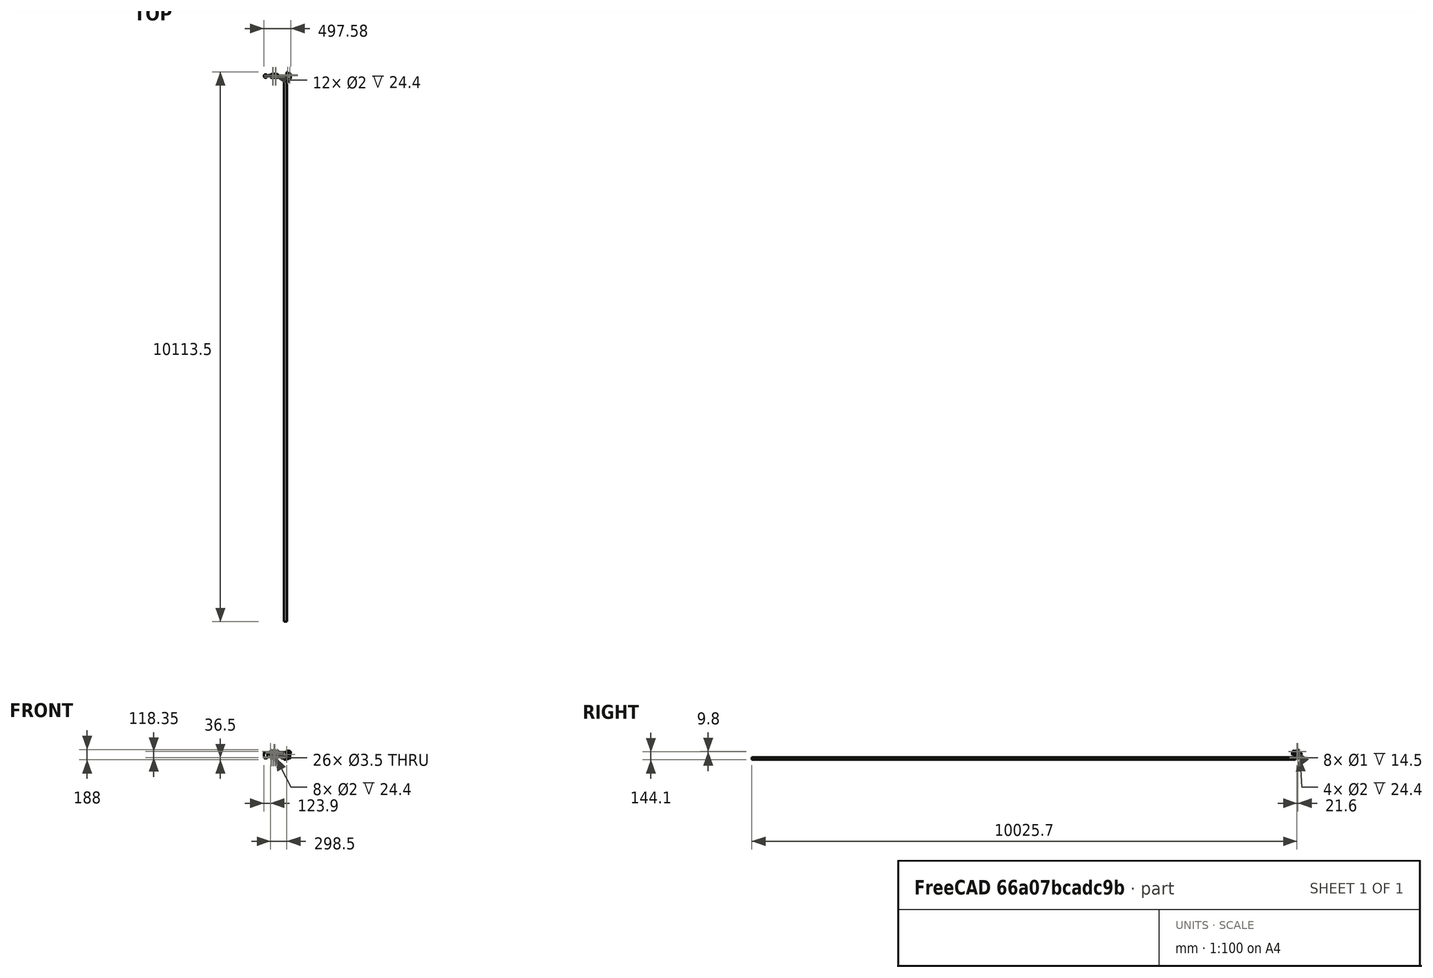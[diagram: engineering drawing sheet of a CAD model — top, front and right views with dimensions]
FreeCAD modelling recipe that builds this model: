
FCSTD DOCUMENT  (FreeCAD 0.15R4671 (Git))
Label: robot completo
License: CC-BY 3.0
LicenseURL: http://creativecommons.org/licenses/by/3.0/
objects: Part::Feature×135, Part::Box×79, Part::Cut×69, Part::Cylinder×67, Part::MultiFuse×45, Part::Fillet×16, Sketcher::SketchObject×16, Part::FeaturePython×12, PartDesign::Pad×11, App::DocumentObjectGroup×10, Part::Mirroring×10, Part::Prism×7, Part::Chamfer×6, PartDesign::Pocket×5, Part::Sphere×3, Mesh::Feature×3, PartDesign::Fillet×2
note: 499 computed .brp shape members not serialized (recipe doc carries the construction recipe); baked Part::Feature solids carry a one-line shape summary decoded from their .brp

FEATURE [Part::Feature] Part__Feature013  label="Servo-D1"
  Placement = pos=(26.5,9.5,100.6) rot=(0,1,0;3.14159rad)
  shape: bbox 55.5 x 20 x 41.74 mm, 365 faces (baked)
FEATURE [Part::Feature] Part__Feature014  label="Servo-D2"
  Placement = pos=(0,0,13) rot=(0.57735,0.57735,0.57735;2.0944rad)
  shape: bbox 41.74 x 55.5 x 20 mm, 365 faces (baked)
FEATURE [Part::Feature] Part__Feature008  label="J1"
  Placement = pos=(-10.8,44.37,77.54) rot=(0.707107,0.707107,0;3.14159rad)
  shape: bbox 11.7 x 15.49 x 2.5 mm, 224 faces (baked)
FEATURE [Part::Feature] Part__Feature009  label="J2"
  Placement = pos=(-10.8,62.15,77.54) rot=(0.707107,0.707107,0;3.14159rad)
  shape: bbox 11.7 x 15.49 x 2.5 mm, 224 faces (baked)
FEATURE [Part::Feature] Part__Feature007  label="J4"
  Placement = pos=(-10.8,59.6199,125.78) rot=(0,0,-1;1.5708rad)
  shape: bbox 11.65 x 20.57 x 2.5 mm, 290 faces (baked)
FEATURE [Part::Feature] Part__Feature010  label="J16"
  Placement = pos=(-9.55,7.19908,100.417) rot=(0.57735,0.57735,-0.57735;2.0944rad)
  shape: bbox 2.94 x 5.43 x 7.98 mm, 414 faces, 0 solids (baked)
FEATURE [Part::Feature] Part__Feature005  label="PCB"
  Placement = pos=(-12.3914,5,75) rot=(0.57735,0.57735,0.57735;2.0944rad)
  shape: bbox 1.591 x 68.6 x 53.36 mm, 426 faces (baked)
FEATURE [Part::Feature] Part__Feature004  label="J010"
  Placement = pos=(-10.8,14.8841,83.3059) rot=(0.707107,0.707107,0;3.14159rad)
  shape: bbox 10.92 x 14.61 x 8.89 mm, 41 faces (baked)
FEATURE [Part::Feature] Part__Feature011  label="U1"
  Placement = pos=(-9.2,12.159,115.511) rot=(0.57735,-0.57735,-0.57735;2.0944rad)
  shape: bbox 2.435 x 26.9 x 13 mm, 503 faces (baked)
FEATURE [Part::Feature] Part__Feature006  label="J8"
  Placement = pos=(-10.8,37.7759,125.78) rot=(0,0,-1;1.5708rad)
  shape: bbox 11.65 x 20.57 x 2.5 mm, 290 faces (baked)
FEATURE [App::DocumentObjectGroup] Group001  label="placa"
  Group = -> [Part__Feature008,Part__Feature009,Part__Feature007,Part__Feature010,Part__Feature005,Part__Feature004,Part__Feature011,Part__Feature006]
FEATURE [Part::Box] Box  label="Cube"
  Height = 24
  Length = 72
  Placement = pos=(-15,-29,-3) rot=(0,0,1;0rad)
  Width = 58
FEATURE [Part::Box] Box001  label="Cube001"
  Height = 25
  Length = 47
  Placement = pos=(-1,-21,2) rot=(0,0,1;0rad)
  Width = 42
FEATURE [Part::Box] Box002  label="Cube002"
  Height = 38
  Length = 28
  Placement = pos=(37,-45,1) rot=(0,0,1;0rad)
  Width = 88
FEATURE [Part::Box] Box003  label="Cube003"
  Height = 38
  Length = 28
  Placement = pos=(-33,-45,1) rot=(0,0,1;0rad)
  Width = 88
FEATURE [Part::Cut] Cut
  Base = -> Box
  Tool = -> Box001
FEATURE [Part::Cut] Cut001
  Base = -> Cut
  Tool = -> Box002
FEATURE [Part::Cut] Cut002
  Base = -> Cut001
  Tool = -> Box003
FEATURE [Part::Box] Box004  label="Cube004"
  Height = 60
  Length = 44
  Placement = pos=(-5,-24,-5) rot=(0,0,1;0rad)
  Width = 61
FEATURE [Part::Mirroring] Part__Mirroring  label="Servo-D1 (Mirror #1)"
  Base = (0,0,0)
  Normal = (0,1,0)
  Placement = pos=(0,72,0) rot=(0,0,1;0rad)
  Source = -> Part__Feature013
FEATURE [Part::Mirroring] Part__Mirroring001  label="Servo-D2 (Mirror #2)"
  Base = (0,0,0)
  Normal = (0,1,0)
  Placement = pos=(0,72,0) rot=(0,0,1;0rad)
  Source = -> Part__Feature014
FEATURE [Part::Cylinder] Cylinder003  label="Joint-D005"
  Angle = 360
  Height = 74.5
  Placement = pos=(-22,9.5,12) rot=(0,1,0;1.5708rad)
  Radius = 1.75
FEATURE [Part::Fillet] Fillet
  Base = -> Cut002
  Edges = 4 edges r=10: [Edge1,Edge3,Edge5,Edge14]
FEATURE [Part::Cylinder] Cylinder002  label="Joint-D004"
  Angle = 360
  Height = 53
  Placement = pos=(-9,9.5,12) rot=(0,1,0;1.5708rad)
  Radius = 10.5
FEATURE [Part::MultiFuse] Fusion
  Shapes = -> [Cylinder002]
FEATURE [Part::Cylinder] Cylinder004  label="Joint-D006"
  Angle = 360
  Height = 74.5
  Placement = pos=(16,9.5,12) rot=(0,1,0;1.5708rad)
  Radius = 5.5
FEATURE [Part::Cut] Cut003
  Base = -> Fusion
  Tool = -> Box004
FEATURE [Part::Cylinder] Cylinder005  label="Joint-D007"
  Angle = 360
  Height = 74.5
  Placement = pos=(-51,9.5,12) rot=(0,1,0;1.5708rad)
  Radius = 1.75
FEATURE [Part::Cut] Cut004
  Base = -> Cut003
  Tool = -> Cylinder004
FEATURE [Part::Cut] Cut005
  Base = -> Cut004
  Tool = -> Cylinder005
FEATURE [Part::Cylinder] Cylinder006  label="Joint-D008"
  Angle = 360
  Height = 74.5
  Placement = pos=(41.8,9.5,12) rot=(0,1,0;1.5708rad)
  Radius = 11
FEATURE [Part::Cut] Cut006
  Base = -> Cut005
  Tool = -> Cylinder006
FEATURE [Part::Cylinder] Cylinder007  label="Joint-D009"
  Angle = 360
  Height = 23.5
  Placement = pos=(16.8,9.5,58.3) rot=(0,1,0;3.14159rad)
  Radius = 11
FEATURE [Part::Cylinder] Cylinder008  label="Joint-D010"
  Angle = 360
  Height = 21.5
  Placement = pos=(16,-24.5,7) rot=(0,1,0;1.5708rad)
  Radius = 1.75
FEATURE [Part::Cylinder] Cylinder009  label="Joint-D011"
  Angle = 360
  Height = 21.5
  Placement = pos=(32,-24.5,7) rot=(0,1,0;1.5708rad)
  Radius = 3
FEATURE [Part::MultiFuse] Fusion001
  Shapes = -> [Cylinder009,Cylinder008]
FEATURE [Part::MultiFuse] Fusion002
  Placement = pos=(0,0,10) rot=(0,0,1;0rad)
  Shapes = -> [Cylinder009,Cylinder008]
FEATURE [Part::MultiFuse] Fusion003
  Placement = pos=(0,49,0) rot=(0,0,1;0rad)
  Shapes = -> [Cylinder009,Cylinder008]
FEATURE [Part::MultiFuse] Fusion004
  Placement = pos=(0,49,10) rot=(0,0,1;0rad)
  Shapes = -> [Cylinder009,Cylinder008]
FEATURE [Part::Box] Box006  label="Cube006"
  Height = 21
  Length = 4
  Placement = pos=(25.5,-28,2) rot=(0,0,1;0rad)
  Width = 56
FEATURE [Part::Cylinder] Cylinder010  label="Joint-D012"
  Angle = 360
  Height = 74.5
  Placement = pos=(17,9.5,12) rot=(0,0,1;0rad)
  Radius = 5.5
FEATURE [Part::Box] Box007  label="Cube007"
  Height = 6
  Length = 3
  Placement = pos=(18.5,-28,4) rot=(0,0,1;0rad)
  Width = 56
FEATURE [Part::Box] Box008  label="Cube008"
  Height = 6
  Length = 3
  Placement = pos=(18.5,-28,14) rot=(0,0,1;0rad)
  Width = 56
FEATURE [Part::Cylinder] Cylinder011  label="Joint-D013"
  Angle = 360
  Height = 74.5
  Placement = pos=(-3,9.5,12) rot=(0,1,0;1.5708rad)
  Radius = 2.75
FEATURE [Part::Box] Box009  label="Cube009"
  Height = 5
  Length = 80
  Placement = pos=(-23,-4,63) rot=(0,0,1;0rad)
  Width = 80
FEATURE [Part::Box] Box010  label="Cube010"
  Height = 9
  Length = 7
  Placement = pos=(-1,-1,63) rot=(0,0,1;0rad)
  Width = 74
FEATURE [Part::Box] Box011  label="Cube011"
  Height = 9
  Length = 7
  Placement = pos=(47,-1,63) rot=(0,0,1;0rad)
  Width = 74
FEATURE [Part::MultiFuse] Fusion005
  Placement = pos=(44,39,98) rot=(0,1,0;1.5708rad)
  Shapes = -> [Cylinder009,Cylinder008]
FEATURE [Part::MultiFuse] Fusion008
  Placement = pos=(44,29,98) rot=(0,1,0;1.5708rad)
  Shapes = -> [Cylinder009,Cylinder008]
FEATURE [Part::MultiFuse] Fusion009
  Placement = pos=(-5,39,98) rot=(0,1,0;1.5708rad)
  Shapes = -> [Cylinder009,Cylinder008]
FEATURE [Part::MultiFuse] Fusion010
  Placement = pos=(-5,29,98) rot=(0,1,0;1.5708rad)
  Shapes = -> [Cylinder009,Cylinder008]
FEATURE [Part::Box] Box012  label="Cube012"
  Height = 9
  Length = 70
  Placement = pos=(-6,8.5,70) rot=(0,0,1;0rad)
  Width = 2
FEATURE [Part::MultiFuse] Fusion011
  Shapes = -> [Box012,Fusion009,Fusion010,Fusion008,Fusion005]
FEATURE [Part::MultiFuse] Fusion012
  Placement = pos=(0,53,0) rot=(0,0,1;0rad)
  Shapes = -> [Box012,Fusion009,Fusion010,Fusion008,Fusion005]
FEATURE [Part::MultiFuse] Fusion013
  Shapes = -> [Box009,Box011,Box010]
FEATURE [Part::Cut] Cut018
  Base = -> Fusion013
  Tool = -> Fusion012
FEATURE [Part::Cut] Cut019
  Base = -> Cut018
  Tool = -> Fusion011
FEATURE [Part::Box] Box014  label="Cube014"
  Height = 43
  Length = 41
  Placement = pos=(6,-1,59) rot=(0,0,1;0rad)
  Width = 21
FEATURE [Part::Box] Box015  label="Cube015"
  Height = 43
  Length = 41
  Placement = pos=(6,52,59) rot=(0,0,1;0rad)
  Width = 21
FEATURE [Part::Cut] Cut020
  Base = -> Cut019
  Tool = -> Box014
FEATURE [Part::Cut] Cut021
  Base = -> Cut020
  Tool = -> Box015
FEATURE [Part::Box] Box016  label="Cube016"
  Height = 12
  Length = 6
  Placement = pos=(-11.5,3,69) rot=(0,0,1;0rad)
  Width = 3
FEATURE [Part::Box] Box017  label="Cube017"
  Height = 12
  Length = 16
  Placement = pos=(-20,-1,63) rot=(0,0,1;0rad)
  Width = 74
FEATURE [Part::Box] Box018  label="Cube018"
  Height = 12
  Length = 6
  Placement = pos=(-11.5,66,69) rot=(0,0,1;0rad)
  Width = 3
FEATURE [Part::MultiFuse] Fusion014
  Shapes = -> [Cut021,Box017]
FEATURE [Part::Cut] Cut022
  Base = -> Fusion014
  Tool = -> Box016
FEATURE [Part::Cut] Cut023
  Base = -> Cut022
  Tool = -> Box018
FEATURE [PartDesign::Fillet] Fillet011  label="horn"
  Placement = pos=(38.5,9.5,13) rot=(0,0,-1;1.5708rad)
  Radius = 0.5
FEATURE [Part::Cylinder] Cylinder021  label="Joint-D014"
  Angle = 360
  Height = 52.5
  Placement = pos=(19,9.5,20.35) rot=(0,1,0;1.5708rad)
  Radius = 1
FEATURE [Part::Cylinder] Cylinder022  label="Joint-D015"
  Angle = 360
  Height = 52.5
  Placement = pos=(19,2,9.5) rot=(0,1,0;1.5708rad)
  Radius = 1
FEATURE [Part::Cylinder] Cylinder023  label="Joint-D016"
  Angle = 360
  Height = 52.5
  Placement = pos=(19,17,9.5) rot=(0,1,0;1.5708rad)
  Radius = 1
FEATURE [Part::MultiFuse] Fusion017
  Placement = pos=(0,0,-1) rot=(0,0,1;0rad)
  Shapes = -> [Cylinder022,Cylinder021,Cylinder023]
FEATURE [Part::MultiFuse] Fusion018
  Placement = pos=(4,0,101) rot=(0,1,0;1.5708rad)
  Shapes = -> [Cylinder022,Cylinder021,Cylinder023]
FEATURE [PartDesign::Fillet] Fillet012  label="horn001"
  Placement = pos=(16.8,9.5,62.5) rot=(-0.57735,0.57735,-0.57735;2.0944rad)
  Radius = 0.5
FEATURE [Part::Mirroring] Part__Mirroring003  label="horn (Mirror #4)"
  Base = (41.6,1.90735e-06,13)
  Normal = (0,1,-1.19209e-07)
  Placement = pos=(0,72,0) rot=(0,0,1;0rad)
  Source = -> Fillet011
FEATURE [Part::Mirroring] Part__Mirroring004  label="horn001 (Mirror #5)"
  Base = (16.8,7.62939e-06,59.3998)
  Normal = (0,1,-1.19209e-07)
  Placement = pos=(0,72,0) rot=(0,0,1;0rad)
  Source = -> Fillet012
FEATURE [Part::Chamfer] Chamfer
  Base = -> Fillet
  Edges = 3 edges r=3: [Edge18,Edge33,Edge37]
FEATURE [Part::Cut] Cut008
  Base = -> Chamfer
  Tool = -> Cylinder003
FEATURE [Part::Cut] Cut010
  Base = -> Cut008
  Tool = -> Box006
FEATURE [Part::Cut] Cut011
  Base = -> Cut010
  Tool = -> Box008
FEATURE [Part::Cut] Cut012
  Base = -> Cut011
  Tool = -> Box007
FEATURE [Part::Cut] Cut013
  Base = -> Cut012
  Tool = -> Fusion004
FEATURE [Part::Cut] Cut014
  Base = -> Cut013
  Tool = -> Fusion003
FEATURE [Part::Cut] Cut015
  Base = -> Cut014
  Tool = -> Fusion002
FEATURE [Part::Cut] Cut016
  Base = -> Cut015
  Tool = -> Fusion001
FEATURE [Part::Cut] Cut017  label="pie"
  Base = -> Cut016
  Tool = -> Cylinder011
FEATURE [Part::Box] Box024  label="Cube024"
  Height = 23
  Length = 6
  Placement = pos=(0,19,7) rot=(0,0,1;0rad)
  Width = 36
FEATURE [Part::Cut] Cut039  label="pie-D"
  Base = -> Cut017
  Placement = pos=(0,0,1) rot=(0,0,1;0rad)
  Tool = -> Box024
FEATURE [Part::Mirroring] Part__Mirroring006  label="pie-I"
  Base = (0,0,0)
  Normal = (0,1,0)
  Placement = pos=(0,72,0) rot=(0,0,1;0rad)
  Source = -> Cut039
FEATURE [Part::Cut] Cut044
  Base = -> Cut006
  Tool = -> Box004
FEATURE [Part::Cut] Cut045
  Base = -> Cut044
  Tool = -> Cylinder007
FEATURE [Part::Cut] Cut046
  Base = -> Cut045
  Tool = -> Fusion018
FEATURE [Part::Cut] Cut047
  Base = -> Cut046
  Tool = -> Fusion017
FEATURE [Part::Cut] Cut048
  Base = -> Cut047
  Placement = pos=(0,0,1) rot=(0,0,1;0rad)
  Tool = -> Cylinder010
FEATURE [Part::Chamfer] Chamfer001
  Base = -> Cut048
  Edges = 1 edges r=4: [Edge61]
FEATURE [Part::Chamfer] Chamfer002  label="pata-D"
  Base = -> Chamfer001
  Edges = 1 edges r=8: [Edge58]
FEATURE [Part::Mirroring] Part__Mirroring007  label="pata-I"
  Base = (17.5,3.8147e-06,32.25)
  Normal = (0,1,-1.19209e-07)
  Placement = pos=(0,72,0) rot=(0,0,1;0rad)
  Source = -> Chamfer002
FEATURE [Part::Cylinder] Cylinder012  label="Cylinder030"
  Angle = 360
  Height = 31
  Placement = pos=(-8.5,92,71.5) rot=(1,0,0;1.5708rad)
  Radius = 1.75
FEATURE [Part::Cut] Cut024
  Base = -> Cut023
  Tool = -> Cylinder012
FEATURE [Part::Cylinder] Cylinder013  label="Cylinder001"
  Angle = 360
  Height = 31
  Placement = pos=(-8.5,11,71.5) rot=(1,0,0;1.5708rad)
  Radius = 1.75
FEATURE [Part::Feature] Part__Feature  label="Portapilas008"
  shape: bbox 2e-07 x 47.97 x 51.59 mm, 1 faces, 0 solids (baked)
FEATURE [Part::Feature] Part__Feature015  label="Portapilas007"
  shape: bbox 9.213 x 1.1 x 48.01 mm, 3 faces, 0 solids (baked)
FEATURE [Part::Feature] Part__Feature016  label="Portapilas006"
  shape: bbox 9.213 x 1.1 x 48.01 mm, 3 faces, 0 solids (baked)
FEATURE [Part::Feature] Part__Feature017  label="Portapilas005"
  shape: bbox 9.213 x 1.1 x 48.01 mm, 3 faces, 0 solids (baked)
FEATURE [Part::Feature] Part__Feature018  label="Portapilas004"
  shape: bbox 9.213 x 1.1 x 48.01 mm, 3 faces, 0 solids (baked)
FEATURE [Part::Feature] Part__Feature019  label="Portapilas003"
  shape: bbox 9.213 x 1.1 x 48.01 mm, 3 faces, 0 solids (baked)
FEATURE [Part::Feature] Part__Feature020  label="Portapilas002"
  shape: bbox 9.213 x 1.1 x 48.01 mm, 3 faces, 0 solids (baked)
FEATURE [Part::Feature] Part__Feature021  label="Portapilas001"
  shape: bbox 16.42 x 48.04 x 51.59 mm, 26 faces, 0 solids (baked)
FEATURE [Part::Feature] Part__Feature022  label="Portapilas"
  shape: bbox 21.03 x 69.14 x 72.63 mm, 394 faces, 0 solids (baked)
FEATURE [Part::MultiFuse] Fusion019  label="peterpilas"
  Placement = pos=(23,77.5,76) rot=(0,0,1;1.5708rad)
  Shapes = -> [Part__Feature022,Part__Feature021,Part__Feature020,Part__Feature019,Part__Feature018,Part__Feature017,Part__Feature016,Part__Feature015,Part__Feature]
FEATURE [Part::Feature] Part__Feature023  label="Ultrasonido_BAT"
  Placement = pos=(-17,36,59.5) rot=(0,0,1;0rad)
  shape: bbox 18.72 x 56 x 27.52 mm, 81 faces (baked)
FEATURE [Part::Cut] Cut050
  Base = -> Cut024
  Tool = -> Cylinder013
FEATURE [Part::Box] Box032  label="Cube032"
  Height = 20
  Length = 3
  Placement = pos=(51,20,66) rot=(0,0,1;0rad)
  Width = 32
FEATURE [Part::Box] Box033  label="Cube033"
  Height = 54
  Length = 4.5
  Placement = pos=(-20,6,64) rot=(0,0,1;0rad)
  Width = 60
FEATURE [Part::Box] Box035  label="Cube035"
  Height = 68
  Length = 6
  Placement = pos=(-23.5,17,68) rot=(0,0,1;0rad)
  Width = 38
FEATURE [Part::Box] Box036  label="Cube034"
  Height = 17
  Length = 13
  Placement = pos=(-14,20,62) rot=(0,0,1;0rad)
  Width = 32
FEATURE [Part::Fillet] Fillet018002
  Base = -> Box036
  Edges = 4 edges r=5: [Edge1,Edge3,Edge5,Edge7]
FEATURE [Part::Cylinder] Cylinder  label="Cylinder094"
  Angle = 360
  Height = 31
  Placement = pos=(-49.5,29,111.5) rot=(0,1,0;1.5708rad)
  Radius = 1.75
FEATURE [Part::Cylinder] Cylinder040  label="Cylinder095"
  Angle = 360
  Height = 31
  Placement = pos=(-49.5,49,91.5) rot=(0,1,0;1.5708rad)
  Radius = 1.75
FEATURE [Part::Cylinder] Cylinder041  label="Cylinder096"
  Angle = 360
  Height = 31
  Placement = pos=(-49.5,49,111.5) rot=(0,1,0;1.5708rad)
  Radius = 1.75
FEATURE [Part::MultiFuse] Fusion025
  Shapes = -> [Box032,Cut050]
FEATURE [Part::Box] Box037  label="Cube036"
  Height = 44
  Length = 61
  Placement = pos=(-9,22,66) rot=(0,0,1;0rad)
  Width = 28
FEATURE [Part::MultiFuse] Fusion026
  Shapes = -> [Fusion025,Box033]
FEATURE [Part::Cut] Cut051
  Base = -> Fusion026
  Tool = -> Fillet018002
FEATURE [Part::Box] Box038  label="Cube037"
  Height = 11
  Length = 8
  Placement = pos=(-11.5,-52,95) rot=(0,0,1;0rad)
  Width = 58
FEATURE [Part::Cylinder] Cylinder042  label="Cylinder097"
  Angle = 360
  Height = 61
  Placement = pos=(-5,124,89.6) rot=(1,0,0;1.5708rad)
  Radius = 4
FEATURE [Part::Cylinder] Cylinder043  label="Cylinder098"
  Angle = 360
  Height = 63
  Placement = pos=(-3,11,83.5) rot=(1,0,0;1.5708rad)
  Radius = 6
FEATURE [Part::Box] Box039  label="Cube038"
  Height = 66
  Length = 76
  Placement = pos=(-21,-2,63) rot=(0,0,1;0rad)
  Width = 76
FEATURE [Part::Cylinder] Cylinder044  label="Cylinder099"
  Angle = 360
  Height = 23
  Placement = pos=(-8.5,1,71.5) rot=(1,0,0;1.5708rad)
  Radius = 1.75
FEATURE [Part::Cylinder] Cylinder045  label="Cylinder100"
  Angle = 360
  Height = 31
  Placement = pos=(-8.5,94,71.5) rot=(1,0,0;1.5708rad)
  Radius = 1.75
FEATURE [Part::Fillet] Fillet018007
  Base = -> Box039
  Edges = 8 edges r=3: [Edge1,Edge2,Edge3,Edge5,Edge6,Edge7,Edge10,Edge12]
FEATURE [Part::Box] Box040  label="Cube039"
  Height = 6
  Length = 81
  Placement = pos=(-23.5,-4.5,63) rot=(0,0,1;0rad)
  Width = 81
FEATURE [Part::Fillet] Fillet018008
  Base = -> Box040
  Edges = 4 edges r=5: [Edge1,Edge3,Edge5,Edge7]
  Placement = pos=(0,0,-1) rot=(0,0,1;0rad)
FEATURE [Part::Cylinder] Cylinder046  label="Cylinder101"
  Angle = 360
  Height = 45
  Placement = pos=(-8.5,-7,71.5) rot=(1,0,0;1.5708rad)
  Radius = 4
FEATURE [Part::Cylinder] Cylinder047  label="Cylinder102"
  Angle = 360
  Height = 45
  Placement = pos=(-8.5,124,71.5) rot=(1,0,0;1.5708rad)
  Radius = 4
FEATURE [Part::MultiFuse] Fusion033
  Shapes = -> [Fillet018007,Fillet018008]
FEATURE [Part::MultiFuse] Fusion034  label="corte-positivo"
  Shapes = -> [Fusion033,Cylinder042,Cylinder047,Cylinder045,Cylinder046,Cylinder043,Box038,Cylinder044]
FEATURE [Part::Cylinder] Cylinder053  label="Cylinder103"
  Angle = 360
  Height = 31
  Placement = pos=(-49.5,29,91.5) rot=(0,1,0;1.5708rad)
  Radius = 1.75
FEATURE [Part::MultiFuse] Fusion038
  Placement = pos=(14,0,0) rot=(0,0,1;0rad)
  Shapes = -> [Cylinder053,Cylinder040,Cylinder041,Cylinder]
FEATURE [App::DocumentObjectGroup] Group004  label="electronic"
  Group = -> [Part__Mirroring,Part__Mirroring001,Part__Mirroring003,Part__Mirroring004,Fusion019,Part__Feature023,Group001]
FEATURE [App::DocumentObjectGroup] Group005  label="aux"
  Group = -> [Fusion034]
FEATURE [Part::Cut] Cut066
  Base = -> Cut051
  Tool = -> Box037
FEATURE [Part::Chamfer] Chamfer003
  Base = -> Cut066
  Edges = 1 edges r=3: [Edge86]
FEATURE [Sketcher::SketchObject] Sketch
  Placement = pos=(-22,0,0) rot=(0.57735,-0.57735,-0.57735;2.0944rad)
  sketch-geometry (4):
    g0: ArcOfCircle CenterX=-49 CenterY=111.5 CenterZ=0 NormalX=0 NormalY=0 NormalZ=1 Radius=3.5 StartAngle=9.1497e-08 EndAngle=3.14159
    g1: LineSegment StartX=-52.5 StartY=111.5 StartZ=0 EndX=-52.5 EndY=91.5 EndZ=0
    g2: LineSegment StartX=-45.5 StartY=111.5 StartZ=0 EndX=-45.5 EndY=91.5 EndZ=0
    g3: ArcOfCircle CenterX=-49 CenterY=91.5 CenterZ=0 NormalX=0 NormalY=0 NormalZ=1 Radius=3.5 StartAngle=3.14159 EndAngle=6.28319
  constraints (13):
    c: DistanceX(g-1,g0) = -49
    c: DistanceY(g-1,g0) = 111.5
    c: Radius(g0) = 3.5
    c: Vertical(g1)
    c: Vertical(g2)
    c: Coincident(g1,g0)
    c: Coincident(g2,g0)
    c: Tangent(g2,g0)
    c: Tangent(g1,g0)
    c: Coincident(g3,g1)
    c: Coincident(g3,g2)
    c: Equal(g3,g0)
    c: Distance(g3,g0) = 20
FEATURE [PartDesign::Pad] Pad
  Length = 5
  Length2 = 100
  Placement = pos=(-22,0,0) rot=(0.57735,-0.57735,-0.57735;2.0944rad)
  Reversed = true
  Sketch = -> Sketch
  Type = 0
FEATURE [Part::FeaturePython] Clone  label="Clone of Pad"  # Draft clone (typed FeaturePython)
  Objects = -> [Pad]
  Placement = pos=(-22,-20,0) rot=(0.57735,-0.57735,-0.57735;2.0944rad)
  Scale = (1,1,1)
FEATURE [Part::MultiFuse] Fusion039
  Placement = pos=(4.5,0,0) rot=(0,0,1;0rad)
  Shapes = -> [Pad,Clone]
FEATURE [Part::MultiFuse] Fusion040
  Shapes = -> [Chamfer003,Fusion039]
FEATURE [Part::Cut] Cut067
  Base = -> Fusion040
  Tool = -> Fusion038
FEATURE [Part::Cut] Cut068
  Base = -> Cut067
  Tool = -> Box035
FEATURE [Sketcher::SketchObject] Sketch001  label="leg-sketch-1"
  Placement = pos=(0,0,0) rot=(0.57735,0.57735,0.57735;2.0944rad)
  sketch-geometry (5):
    g0: LineSegment StartX=-49 StartY=10.5 StartZ=0 EndX=0 EndY=10.5 EndZ=0
    g1: LineSegment StartX=0 StartY=10.5 StartZ=0 EndX=0 EndY=-10.5 EndZ=0
    g2: LineSegment StartX=0 StartY=-10.5 StartZ=0 EndX=-49 EndY=-10.5 EndZ=0
    g3: LineSegment [constr] StartX=-49 StartY=-10.5 StartZ=0 EndX=-49 EndY=10.5 EndZ=0
    g4: ArcOfCircle CenterX=-49 CenterY=0 CenterZ=0 NormalX=0 NormalY=0 NormalZ=1 Radius=10.5 StartAngle=1.5708 EndAngle=4.71239
  constraints (15):
    c: Coincident(g0,g1)
    c: Coincident(g1,g2)
    c: Coincident(g2,g3)
    c: Coincident(g3,g0)
    c: Horizontal(g0)
    c: Horizontal(g2)
    c: Vertical(g1)
    c: Vertical(g3)
    c: PointOnObject(g4,g3)
    c: Coincident(g4,g0)
    c: Coincident(g4,g2)
    c: PointOnObject(g4,g-1)
    c: PointOnObject(g0,g-2)
    c: DistanceX(g0) = 49
    c: DistanceY(g1) = -21
FEATURE [PartDesign::Pad] Pad001  label="leg-block-1"
  Length = 53
  Length2 = 100
  Midplane = true
  Placement = pos=(0,0,0) rot=(0.57735,0.57735,0.57735;2.0944rad)
  Sketch = -> Sketch001
  Type = 0
FEATURE [Sketcher::SketchObject] Sketch002  label="leg-top-sketch"
  ExternalGeometry = -> [Pad001]
  Placement = pos=(0,0,10.5) rot=(0,0,-1;1.5708rad)
  Support = -> Pad001 [Face1]
  sketch-geometry (9):
    g0: LineSegment StartX=64 StartY=21.5 StartZ=0 EndX=10 EndY=21.5 EndZ=0
    g1: LineSegment StartX=6 StartY=17.5 StartZ=0 EndX=6 EndY=-19.5 EndZ=0
    g2: LineSegment StartX=9 StartY=-22.5 StartZ=0 EndX=64 EndY=-22.5 EndZ=0
    g3: LineSegment StartX=64 StartY=-22.5 StartZ=0 EndX=64 EndY=21.5 EndZ=0
    g4: LineSegment StartX=6 StartY=17.5 StartZ=0 EndX=10 EndY=21.5 EndZ=0
    g5: LineSegment [constr] StartX=6 StartY=17.5 StartZ=0 EndX=6 EndY=21.5 EndZ=0
    g6: LineSegment StartX=6 StartY=-19.5 StartZ=0 EndX=9 EndY=-22.5 EndZ=0
    g7: LineSegment [constr] StartX=9 StartY=-22.5 StartZ=0 EndX=6 EndY=-22.5 EndZ=0
    g8: LineSegment [constr] StartX=6 StartY=-22.5 StartZ=0 EndX=6 EndY=-19.5 EndZ=0
  constraints (26):
    c: Coincident(g2,g3)
    c: Coincident(g3,g0)
    c: Horizontal(g0)
    c: Horizontal(g2)
    c: Vertical(g1)
    c: Vertical(g3)
    c: DistanceY(g-3,g5) = -5
    c: DistanceY(g7,g-4) = -4
    c: Angle(g-2,g4) = 2.35619
    c: Coincident(g1,g4)
    c: Coincident(g5,g1)
    c: Vertical(g5)
    c: DistanceY(g1,g7) = -40
    c: DistanceX(g5,g-3) = -6
    c: Coincident(g0,g4)
    c: PointOnObject(g5,g0)
    c: DistanceX(g-3,g0) = 15
    c: Coincident(g2,g6)
    c: Coincident(g7,g2)
    c: Horizontal(g7)
    c: DistanceX(g7) = -3
    c: Coincident(g1,g6)
    c: Coincident(g8,g7)
    c: Coincident(g8,g1)
    c: Equal(g8,g7)
    c: Vertical(g8)
FEATURE [PartDesign::Pocket] Pocket  label="leg-block-2"
  Length = 5
  Placement = pos=(0,0,0) rot=(0.57735,0.57735,0.57735;2.0944rad)
  Sketch = -> Sketch002
  Type = 1
FEATURE [Sketcher::SketchObject] Sketch003  label="ankle-rounded-horn-sketch"
  ExternalGeometry = -> [Pocket]
  Placement = pos=(26.5,0,0) rot=(0.57735,0.57735,0.57735;2.0944rad)
  Support = -> Pocket [Face4]
  sketch-geometry (1):
    g0: Circle CenterX=-49 CenterY=0 CenterZ=0 NormalX=0 NormalY=0 NormalZ=1 Radius=10.75
  constraints (2):
    c: Coincident(g0,g-3)
    c: Radius(g0) = 10.75
FEATURE [PartDesign::Pocket] Pocket001  label="ankle-rounded-horn-cutout"
  Length = 2.2
  Placement = pos=(0,0,0) rot=(0.57735,0.57735,0.57735;2.0944rad)
  Sketch = -> Sketch003
  Type = 0
FEATURE [Sketcher::SketchObject] Sketch004  label="ankle-rear-shaft-drill-sketch"
  ExternalGeometry = -> [Pocket001]
  Placement = pos=(-26.5,0,0) rot=(0.57735,0.57735,-0.57735;4.18879rad)
  Support = -> Pocket001 [Face2]
  sketch-geometry (1):
    g0: Circle CenterX=-49 CenterY=0 CenterZ=0 NormalX=0 NormalY=0 NormalZ=1 Radius=1.75
  constraints (2):
    c: Coincident(g0,g-3)
    c: Radius(g0) = 1.75
FEATURE [PartDesign::Pocket] Pocket002  label="ankle-rear-shaft-drill"
  Length = 0
  Placement = pos=(0,0,0) rot=(0.57735,0.57735,0.57735;2.0944rad)
  Sketch = -> Sketch004
  Type = 2
FEATURE [Sketcher::SketchObject] Sketch005  label="hip-rounded-horn-cutout-sketch"
  Placement = pos=(0,-6,0) rot=(-0.57735,-0.57735,0.57735;4.18879rad)
  Support = -> Pocket002 [Face10]
  sketch-geometry (1):
    g0: Circle CenterX=0 CenterY=0 CenterZ=0 NormalX=0 NormalY=0 NormalZ=1 Radius=11
  constraints (2):
    c: Coincident(g0,g-1)
    c: Radius(g0) = 11
FEATURE [PartDesign::Pocket] Pocket003  label="hip-rounded-horn-cutout"
  Length = 3.3
  Placement = pos=(0,0,0) rot=(0.57735,0.57735,0.57735;2.0944rad)
  Sketch = -> Sketch005
  Type = 0
FEATURE [Sketcher::SketchObject] Sketch006  label="horn-side-chamfer-sketch"
  ExternalGeometry = -> [Pocket003]
  Placement = pos=(0,0,10.5) rot=(0,0,-1;1.5708rad)
  Support = -> Pocket003 [Face1]
  sketch-geometry (3):
    g0: LineSegment StartX=0 StartY=18.5 StartZ=0 EndX=8 EndY=26.5 EndZ=0
    g1: LineSegment StartX=0 StartY=18.5 StartZ=0 EndX=0 EndY=26.5 EndZ=0
    g2: LineSegment StartX=0 StartY=26.5 StartZ=0 EndX=8 EndY=26.5 EndZ=0
  constraints (8):
    c: PointOnObject(g0,g-2)
    c: PointOnObject(g0,g-3)
    c: Angle(g-2,g0) = 2.35619
    c: DistanceY(g-3,g0) = -8
    c: Coincident(g0,g1)
    c: Coincident(g1,g-3)
    c: Coincident(g1,g2)
    c: Coincident(g2,g0)
FEATURE [PartDesign::Pocket] Pocket004  label="horn-side-chamfer"
  Length = 5
  Placement = pos=(0,0,0) rot=(0.57735,0.57735,0.57735;2.0944rad)
  Sketch = -> Sketch006
  Type = 1
FEATURE [Part::Cylinder] Cylinder054  label="servo-shaft-drill"
  Angle = 360
  Height = 20
  Placement = pos=(0,10,0) rot=(1,0,0;1.5708rad)
  Radius = 5.5
FEATURE [Part::Cylinder] Cylinder055  label="servo-horn-small-drill-master"
  Angle = 360
  Height = 20
  Placement = pos=(-3.5,10,7.5) rot=(1,0,0;1.5708rad)
  Radius = 1
FEATURE [Part::FeaturePython] Clone001  label="Clone of servo-horn-small-drill-master"  # Draft clone (typed FeaturePython)
  Objects = -> [Cylinder055]
  Placement = pos=(7.35,10,-2.33815e-06) rot=(1,0,0;1.5708rad)
  Scale = (1,1,1)
FEATURE [Part::FeaturePython] Clone002  label="Clone of servo-horn-small-drill-master001"  # Draft clone (typed FeaturePython)
  Objects = -> [Cylinder055]
  Placement = pos=(-3.5,10,-7.5) rot=(1,0,0;1.5708rad)
  Scale = (1,1,1)
FEATURE [Part::MultiFuse] Fusion041  label="servo-Drills-block1-master"
  Shapes = -> [Clone001,Clone002,Cylinder055,Cylinder054]
FEATURE [Part::FeaturePython] Clone003  label="Clone of servo-Drills-block1-master"  # Draft clone (typed FeaturePython)
  Objects = -> [Fusion041]
  Placement = pos=(22,-49,6.96015e-06) rot=(0,0,1;1.5708rad)
  Scale = (1,1,1)
FEATURE [Part::MultiFuse] Fusion042  label="Servo-horn-drills"
  Shapes = -> [Fusion041,Clone003]
FEATURE [Part::Cut] Cut070  label="Leg"
  Base = -> Pocket004
  Tool = -> Fusion042
FEATURE [App::DocumentObjectGroup] Group007  label="Leg-src"
  Group = -> [Pad001,Pocket,Pocket001,Pocket002,Pocket003,Cut070]
FEATURE [App::DocumentObjectGroup] Group006  label="src"
  Group = -> [Group007]
FEATURE [Part::Feature] Fusion043  label="soft-drink-can"
  Placement = pos=(-397.85,47.19,0) rot=(0,0,-1;1.5708rad)
  shape: bbox 66.1 x 66.1 x 115.2 mm, 53 faces (baked)
FEATURE [App::DocumentObjectGroup] Group018  label="development"
  Group = -> [Group006]
FEATURE [Part::Fillet] Fillet018013  label="chass"
  Base = -> Cut068
  Edges = 4 edges r=3: [Edge75,Edge118,Edge216,Edge229]
FEATURE [Sketcher::SketchObject] Sketch010
  Placement = pos=(-1,0,0) rot=(0.57735,0.57735,0.57735;2.0944rad)
  sketch-geometry (5):
    g0: LineSegment StartX=-35.7295 StartY=116.767 StartZ=0 EndX=-15.7739 EndY=107.988 EndZ=0
    g1: LineSegment StartX=-7.00034 StartY=107.988 StartZ=0 EndX=-7.00034 EndY=136.643 EndZ=0
    g2: LineSegment StartX=-7.00034 StartY=136.643 StartZ=0 EndX=-31.551 EndY=136.643 EndZ=0
    g3: ArcOfCircle CenterX=-31.551 CenterY=126.266 CenterZ=0 NormalX=0 NormalY=0 NormalZ=1 Radius=10.3774 StartAngle=1.5708 EndAngle=4.29797
    g4: LineSegment StartX=-15.7739 StartY=107.988 StartZ=0 EndX=-7.00034 EndY=107.988 EndZ=0
  constraints (10):
    c: Coincident(g1,g2)
    c: Coincident(g2,g3)
    c: Coincident(g0,g3)
    c: Horizontal(g2)
    c: Vertical(g1)
    c: Tangent(g3,g0)
    c: Tangent(g3,g2)
    c: Coincident(g1,g4)
    c: Coincident(g0,g4)
    c: Horizontal(g4)
FEATURE [PartDesign::Pad] Pad005
  Length = 42
  Length2 = 100
  Placement = pos=(-1,0,0) rot=(0.57735,0.57735,0.57735;2.0944rad)
  Sketch = -> Sketch010
  Type = 0
FEATURE [Part::MultiFuse] Fusion045  label="servo-src"
  Placement = pos=(23,4.5,120) rot=(0,0.707107,-0.707107;3.14159rad)
  Shapes = -> [Part__Feature,Part__Feature004,Part__Feature005]
FEATURE [Part::FeaturePython] Clone007  label="microservo"  # Draft clone (typed FeaturePython)
  Objects = -> [Fusion045]
  Placement = pos=(-207.5,47,122.5) rot=(0.57735,0.57735,0.57735;2.0944rad)
  Scale = (1,1,1)
FEATURE [Part::FeaturePython] Clone008  label="microservo001"  # Draft clone (typed FeaturePython)
  Objects = -> [Fusion045]
  Placement = pos=(-270.5,47,122.5) rot=(0.57735,0.57735,-0.57735;4.18879rad)
  Scale = (1,1,1)
FEATURE [Part::FeaturePython] Clone009  label="microservo002"  # Draft clone (typed FeaturePython)
  Objects = -> [Fusion045]
  Placement = pos=(-307,51.5,122.5) rot=(0.57735,-0.57735,0.57735;2.0944rad)
  Scale = (1,1,1)
FEATURE [Sketcher::SketchObject] Sketch012
  Placement = pos=(3,-12,-1) rot=(0.57735,0.57735,0.57735;2.0944rad)
  sketch-geometry (4):
    g0: LineSegment StartX=-4.88207 StartY=101.941 StartZ=0 EndX=-4.88207 EndY=138.56 EndZ=0
    g1: LineSegment StartX=-4.88207 StartY=138.56 StartZ=0 EndX=-40.5711 EndY=142.374 EndZ=0
    g2: LineSegment StartX=-40.5711 StartY=142.374 StartZ=0 EndX=-40.5711 EndY=120.688 EndZ=0
    g3: LineSegment StartX=-40.5711 StartY=120.688 StartZ=0 EndX=-4.88207 EndY=101.941 EndZ=0
  constraints (6):
    c: Coincident(g0,g1)
    c: Coincident(g1,g2)
    c: Coincident(g2,g3)
    c: Coincident(g0,g3)
    c: Vertical(g0)
    c: Vertical(g2)
FEATURE [PartDesign::Pad] Pad007
  Length = 34
  Length2 = 100
  Placement = pos=(3,-12,-1) rot=(0.57735,0.57735,0.57735;2.0944rad)
  Sketch = -> Sketch012
  Type = 0
FEATURE [Part::Cut] Cut085
  Base = -> Pad005
  Tool = -> Pad007
FEATURE [Part::Cylinder] Cylinder056  label="Cilindro"
  Angle = 360
  Height = 10
  Placement = pos=(17.25,-4,120) rot=(1,0,0;1.5708rad)
  Radius = 10
FEATURE [Part::Cut] Cut086
  Base = -> Cut085
  Tool = -> Cylinder056
FEATURE [Part::Cylinder] Cylinder057  label="Cilindro001"
  Angle = 360
  Height = 13
  Placement = pos=(17.25,-6,120) rot=(1,0,0;1.5708rad)
  Radius = 3
FEATURE [Part::Cut] Cut087
  Base = -> Cut086
  Tool = -> Cylinder057
FEATURE [Part::Chamfer] Chamfer104
  Base = -> Cut087
  Edges = 1 edges r=1: [Edge10]
FEATURE [Part::Cylinder] Cylinder058  label="Cilindro002"
  Angle = 360
  Height = 22
  Placement = pos=(20.25,-32,125.75) rot=(0,1,0;1.5708rad)
  Radius = 3
FEATURE [Part::Cut] Cut088
  Base = -> Chamfer104
  Tool = -> Cylinder058
FEATURE [Part::Cylinder] Cylinder059  label="Cilindro003"
  Angle = 360
  Height = 22
  Placement = pos=(20.25,-34,132.75) rot=(0,1,0;1.5708rad)
  Radius = 1.25
FEATURE [Part::Cylinder] Cylinder060  label="Cilindro004"
  Angle = 360
  Height = 22
  Placement = pos=(20.25,-30,118.75) rot=(0,1,0;1.5708rad)
  Radius = 1.25
FEATURE [Part::Cylinder] Cylinder061  label="Cilindro005"
  Angle = 360
  Height = 22
  Placement = pos=(20.25,-38,124.25) rot=(0,1,0;1.5708rad)
  Radius = 1.25
FEATURE [Part::Cylinder] Cylinder062  label="Cilindro006"
  Angle = 360
  Height = 22
  Placement = pos=(20.25,-26,127.25) rot=(0,1,0;1.5708rad)
  Radius = 1.25
FEATURE [Part::MultiFuse] Fusion046
  Shapes = -> [Cylinder059,Cylinder061,Cylinder062,Cylinder060]
FEATURE [Part::Cylinder] Cylinder063  label="Cilindro007"
  Angle = 360
  Height = 22
  Placement = pos=(20.25,-34,132.75) rot=(0,1,0;1.5708rad)
  Radius = 1.25
FEATURE [Part::Cylinder] Cylinder064  label="Cilindro008"
  Angle = 360
  Height = 22
  Placement = pos=(20.25,-30,118.75) rot=(0,1,0;1.5708rad)
  Radius = 1.25
FEATURE [Part::Cylinder] Cylinder065  label="Cilindro009"
  Angle = 360
  Height = 22
  Placement = pos=(20.25,-38,124.25) rot=(0,1,0;1.5708rad)
  Radius = 1.25
FEATURE [Part::Cylinder] Cylinder066  label="Cilindro010"
  Angle = 360
  Height = 22
  Placement = pos=(20.25,-26,127.25) rot=(0,1,0;1.5708rad)
  Radius = 1.25
FEATURE [Part::MultiFuse] Fusion047
  Placement = pos=(114.108,21,33.6462) rot=(0.280624,-0.280624,-0.917878;1.65638rad)
  Shapes = -> [Cylinder063,Cylinder065,Cylinder066,Cylinder064]
FEATURE [Part::Cut] Cut089
  Base = -> Cut088
  Tool = -> Fusion047
FEATURE [Part::Cut] Cut090
  Base = -> Cut089
  Tool = -> Fusion046
FEATURE [Part::Cylinder] Cylinder067  label="Cilindro011"
  Angle = 360
  Height = 22
  Placement = pos=(-4.75,-32,125.75) rot=(0,1,0;1.5708rad)
  Radius = 1.75
FEATURE [Part::Cut] Cut091  label="shoulder-src"
  Base = -> Cut090
  Tool = -> Cylinder067
FEATURE [Part::FeaturePython] Clone011  label="microservo003"  # Draft clone (typed FeaturePython)
  Objects = -> [Clone009]
  Placement = pos=(-171,51.5,122.5) rot=(0.57735,-0.57735,0.57735;2.0944rad)
  Scale = (1,1,1)
FEATURE [Part::Box] Box054  label="Cubo004"
  Height = 56
  Length = 19
  Placement = pos=(4,98,80) rot=(0,0,1;0rad)
  Width = 15
FEATURE [Part::Cylinder] Cylinder073  label="Cilindro014"
  Angle = 360
  Height = 32
  Placement = pos=(8,90,84) rot=(-1,0,0;1.5708rad)
  Radius = 1.75
FEATURE [Part::Cylinder] Cylinder074  label="Cilindro015"
  Angle = 360
  Height = 32
  Placement = pos=(18,90,84) rot=(-1,0,0;1.5708rad)
  Radius = 1.75
FEATURE [Part::MultiFuse] Fusion056
  Shapes = -> [Cylinder074,Cylinder073]
FEATURE [Part::Cut] Cut098
  Base = -> Box054
  Tool = -> Fusion056
FEATURE [Sketcher::SketchObject] Sketch015
  Placement = pos=(38,-16,143.25) rot=(0,1,0;1.5708rad)
  sketch-geometry (7):
    g0: Circle CenterX=37 CenterY=120 CenterZ=0 NormalX=0 NormalY=0 NormalZ=1 Radius=1
    g1: Circle CenterX=9.5 CenterY=120 CenterZ=0 NormalX=0 NormalY=0 NormalZ=1 Radius=1
    g2: LineSegment StartX=35.25 StartY=126.5 StartZ=0 EndX=11.25 EndY=126.5 EndZ=0
    g3: LineSegment StartX=11.25 StartY=126.5 StartZ=0 EndX=11.25 EndY=113.5 EndZ=0
    g4: LineSegment StartX=11.25 StartY=113.5 StartZ=0 EndX=35.25 EndY=113.5 EndZ=0
    g5: LineSegment StartX=35.25 StartY=113.5 StartZ=0 EndX=35.25 EndY=126.5 EndZ=0
    g6: LineSegment [constr] StartX=9.5 StartY=120 StartZ=0 EndX=37 EndY=120 EndZ=0
  constraints (20):
    c: Coincident(g2,g3)
    c: Coincident(g3,g4)
    c: Coincident(g4,g5)
    c: Coincident(g5,g2)
    c: Horizontal(g2)
    c: Horizontal(g4)
    c: Vertical(g3)
    c: Vertical(g5)
    c: Distance(g2) = 24
    c: Distance(g5) = 13
    c: Radius(g1) = 1
    c: Equal(g1,g0)
    c: Coincident(g0,g6)
    c: Coincident(g1,g6)
    c: Distance(g6) = 27.5
    c: Horizontal(g6)
    c: DistanceX(g-1,g1) = 9.5
    c: DistanceY(g1) = 120
    c: DistanceY(g1,g3) = -6.5
    c: DistanceX(g1,g2) = 1.75
FEATURE [PartDesign::Pad] Pad010
  Length = 30
  Length2 = 100
  Placement = pos=(38,-16,143.25) rot=(0,1,0;1.5708rad)
  Reversed = true
  Sketch = -> Sketch015
  Type = 0
FEATURE [Part::Cut] Cut099
  Base = -> Cut098
  Tool = -> Pad010
FEATURE [Part::Chamfer] Chamfer108
  Base = -> Cut099
  Edges = 2 edges r=3: [Edge2,Edge14]
FEATURE [Part::Cylinder] Cylinder075  label="Cilindro016"
  Angle = 360
  Height = 32
  Placement = pos=(-5,104,125.85) rot=(-0.57735,0.57735,-0.57735;2.0944rad)
  Radius = 1.75
FEATURE [Part::Prism] Prism001  label="Prisma"
  Circumradius = 3.3
  Height = 10
  Placement = pos=(6,104,125.85) rot=(-0.57735,0.57735,-0.57735;2.0944rad)
  Polygon = 6
FEATURE [Part::MultiFuse] Fusion057
  Shapes = -> [Prism001,Cylinder075]
FEATURE [Part::Cut] Cut100  label="arm-src"
  Base = -> Chamfer108
  Tool = -> Fusion057
FEATURE [Part::Box] Box057  label="Cube078"
  Height = 66
  Length = 76
  Placement = pos=(-21,-2,87) rot=(0,0,1;0rad)
  Width = 76
FEATURE [Part::Fillet] Fillet018013003
  Base = -> Box057
  Edges = 8 edges r=3.5: [Edge1,Edge2,Edge3,Edge5,Edge6,Edge7,Edge10,Edge12]
  Placement = pos=(0,0,-24) rot=(0,0,1;0rad)
FEATURE [Part::Cylinder] Cylinder078  label="Cylinder105"
  Angle = 360
  Height = 31
  Placement = pos=(-8.5,11,71.5) rot=(1,0,0;1.5708rad)
  Radius = 1.75
FEATURE [Part::Cylinder] Cylinder079  label="Cylinder106"
  Angle = 360
  Height = 31
  Placement = pos=(-8.5,80,71.5) rot=(1,0,0;1.5708rad)
  Radius = 1.75
FEATURE [Part::Cylinder] Cylinder080  label="Cylinder107"
  Angle = 360
  Height = 31
  Placement = pos=(-4,11,83.5) rot=(1,0,0;1.5708rad)
  Radius = 6
FEATURE [Part::Box] Box058  label="Cube079"
  Height = 11
  Length = 8
  Placement = pos=(-13.5,-13,95) rot=(0,0,1;0rad)
  Width = 24
FEATURE [Part::Cylinder] Cylinder083  label="Cylinder108"
  Angle = 360
  Height = 31
  Placement = pos=(-7,80,89.6) rot=(1,0,0;1.5708rad)
  Radius = 4
FEATURE [Part::Box] Box059  label="Cube080"
  Height = 49
  Length = 17
  Placement = pos=(-14,-2.5,75) rot=(0,0,1;0rad)
  Width = 77
FEATURE [Part::Fillet] Fillet018013005
  Base = -> Box059
  Edges = 12 edges r=2: [Edge1,Edge2,Edge3,Edge4,Edge5,Edge6,Edge7,Edge8,Edge9,Edge10,Edge11,Edge12]
FEATURE [Part::Box] Box060  label="Cubo007"
  Height = 63
  Length = 80
  Placement = pos=(-23,-4,68) rot=(0,0,1;0rad)
  Width = 80
FEATURE [Part::Cut] Cut103
  Base = -> Box060
  Tool = -> Fillet018013003
FEATURE [Part::MultiFuse] Fusion061
  Shapes = -> [Box058,Cylinder080,Cylinder078,Fillet018013005,Cylinder083,Cylinder079]
FEATURE [Part::Cut] Cut104
  Base = -> Cut103
  Tool = -> Fusion061
FEATURE [Sketcher::SketchObject] Sketch017
  Placement = pos=(-0.25,-35,0) rot=(1,0,0;1.5708rad)
  sketch-geometry (7):
    g0: Circle CenterX=37 CenterY=120 CenterZ=0 NormalX=0 NormalY=0 NormalZ=1 Radius=1.2
    g1: Circle CenterX=9.5 CenterY=120 CenterZ=0 NormalX=0 NormalY=0 NormalZ=1 Radius=1.2
    g2: LineSegment StartX=35.25 StartY=126.5 StartZ=0 EndX=11.25 EndY=126.5 EndZ=0
    g3: LineSegment StartX=11.25 StartY=126.5 StartZ=0 EndX=11.25 EndY=113.5 EndZ=0
    g4: LineSegment StartX=11.25 StartY=113.5 StartZ=0 EndX=35.25 EndY=113.5 EndZ=0
    g5: LineSegment StartX=35.25 StartY=113.5 StartZ=0 EndX=35.25 EndY=126.5 EndZ=0
    g6: LineSegment [constr] StartX=9.5 StartY=120 StartZ=0 EndX=37 EndY=120 EndZ=0
  constraints (20):
    c: Coincident(g2,g3)
    c: Coincident(g3,g4)
    c: Coincident(g4,g5)
    c: Coincident(g5,g2)
    c: Horizontal(g2)
    c: Horizontal(g4)
    c: Vertical(g3)
    c: Vertical(g5)
    c: Distance(g2) = 24
    c: Distance(g5) = 13
    c: Radius(g1) = 1.2
    c: Equal(g1,g0)
    c: Coincident(g0,g6)
    c: Coincident(g1,g6)
    c: Distance(g6) = 27.5
    c: Horizontal(g6)
    c: DistanceX(g-1,g1) = 9.5
    c: DistanceY(g1) = 120
    c: DistanceY(g1,g3) = -6.5
    c: DistanceX(g1,g2) = 1.75
FEATURE [PartDesign::Pad] Pad012
  Length = 140
  Length2 = 100
  Placement = pos=(-0.25,-35,0) rot=(1,0,0;1.5708rad)
  Reversed = true
  Sketch = -> Sketch017
  Type = 0
FEATURE [Part::Box] Box061  label="Cubo008"
  Height = 4
  Length = 14
  Placement = pos=(11,75.5,109) rot=(0,0,1;0rad)
  Width = 3
FEATURE [Part::Box] Box062  label="Cubo009"
  Height = 4
  Length = 14
  Placement = pos=(11,75.5,127) rot=(0,0,1;0rad)
  Width = 3
FEATURE [Part::Box] Box063  label="Cubo010"
  Height = 4
  Length = 14
  Placement = pos=(11,-6.5,109) rot=(0,0,1;0rad)
  Width = 3
FEATURE [Part::Box] Box064  label="Cubo011"
  Height = 4
  Length = 14
  Placement = pos=(11,-6.5,127) rot=(0,0,1;0rad)
  Width = 3
FEATURE [Part::Cut] Cut105
  Base = -> Cut104
  Tool = -> Pad012
FEATURE [Part::MultiFuse] Fusion062
  Shapes = -> [Cut105,Box062,Box061,Box063,Box064]
FEATURE [Part::Fillet] Fillet018013006  label="prebody"
  Base = -> Fusion062
  Edges = 8 edges r=1: [Edge2,Edge4,Edge64,Edge66,Edge160,Edge165,Edge170,Edge174]
FEATURE [Part::FeaturePython] Clone022  label="head-servo"  # Draft clone (typed FeaturePython)
  Objects = -> [Clone009]
  Placement = pos=(-239,46.75,151) rot=(0.707107,0.707107,0;3.14159rad)
  Scale = (1,1,1)
FEATURE [Part::Feature] Pocket005  label="shaft-drill001"
  Placement = pos=(-171,34.6,128.25) rot=(1,0,0;1.5708rad)
  shape: bbox 18.7 x 4.1 x 18.7 mm, 22 faces (baked)
FEATURE [Part::Box] Box065  label="Cubo"
  Height = 4
  Length = 10
  Placement = pos=(13,-11,104) rot=(0,0,1;0rad)
  Width = 94
FEATURE [Part::Cut] Cut107  label="body-src"
  Base = -> Fillet018013006
  Tool = -> Box065
FEATURE [Part::Feature] Compound  label="Servo-Futaba-3003-ready002"
  Placement = pos=(-203,69.69,14.95) rot=(0,0.707107,-0.707107;3.14159rad)
  shape: bbox 57.75 x 41.74 x 20 mm, 378 faces, 4 solids (baked)
FEATURE [Part::Feature] Chamfer109  label="ISO4762_Hex_screw-M3x020"
  Placement = pos=(-227.45,37.49,20) rot=(0.57735,0.57735,-0.57735;2.0944rad)
  shape: bbox 5.5 x 19 x 5.5 mm, 16 faces (baked)
FEATURE [Part::Feature] Chamfer110  label="ISO4762_Hex_screw-M3x023"
  Placement = pos=(-227.45,37.49,10) rot=(0.57735,0.57735,-0.57735;2.0944rad)
  shape: bbox 5.5 x 19 x 5.5 mm, 16 faces (baked)
FEATURE [Part::Feature] Chamfer111  label="ISO4032-Hex-Nut-M008"
  Placement = pos=(-227.45,48.69,10) rot=(0,0,1;0rad)
  shape: bbox 6.35 x 2.4 x 6.35 mm, 29 faces (baked)
FEATURE [Part::Feature] Chamfer112  label="ISO4032-Hex-Nut-M007"
  Placement = pos=(-227.45,48.49,20) rot=(0,0,1;0rad)
  shape: bbox 6.35 x 2.4 x 6.35 mm, 29 faces (baked)
FEATURE [Part::Feature] Chamfer113  label="ISO-10642-M3x011"
  Placement = pos=(-212.45,70.2132,15) rot=(0.57735,0.57735,-0.57735;2.0944rad)
  shape: bbox 6.046 x 10 x 6.046 mm, 25 faces (baked)
FEATURE [Part::Feature] Chamfer114  label="ISO4762_Hex_screw-M3x022"
  Placement = pos=(-178.45,37.49,20) rot=(0.57735,0.57735,-0.57735;2.0944rad)
  shape: bbox 5.5 x 19 x 5.5 mm, 16 faces (baked)
FEATURE [Part::Feature] Chamfer115  label="ISO4032-Hex-Nut-M010"
  Placement = pos=(-178.45,48.49,20) rot=(0,0,1;0rad)
  shape: bbox 6.35 x 2.4 x 6.35 mm, 29 faces (baked)
FEATURE [Part::Feature] Chamfer116  label="ISO4032-Hex-Nut-M009"
  Placement = pos=(-178.45,48.49,10) rot=(0,0,1;0rad)
  shape: bbox 6.35 x 2.4 x 6.35 mm, 29 faces (baked)
FEATURE [Part::Feature] Chamfer117  label="ISO4762_Hex_screw-M3x021"
  Placement = pos=(-178.45,37.49,10) rot=(0.57735,0.57735,-0.57735;2.0944rad)
  shape: bbox 5.5 x 19 x 5.5 mm, 16 faces (baked)
FEATURE [Part::Feature] Chamfer118  label="ISO-10642-M3x10"
  Placement = pos=(-265.35,70.0132,15) rot=(0.57735,0.57735,-0.57735;2.0944rad)
  shape: bbox 6.046 x 10 x 6.046 mm, 25 faces (baked)
FEATURE [Part::Feature] Chamfer119  label="ISO4032-Hex-Nut-M3"
  Placement = pos=(-250.35,48.29,20) rot=(0,0,1;0rad)
  shape: bbox 6.35 x 2.4 x 6.35 mm, 29 faces (baked)
FEATURE [Part::Feature] Chamfer120  label="ISO4032-Hex-Nut-M004"
  Placement = pos=(-250.35,47.69,10) rot=(0,0,1;0rad)
  shape: bbox 6.35 x 2.4 x 6.35 mm, 29 faces (baked)
FEATURE [Part::Feature] Chamfer121  label="ISO4032-Hex-Nut-M005"
  Placement = pos=(-299.35,47.69,20) rot=(0,0,1;0rad)
  shape: bbox 6.35 x 2.4 x 6.35 mm, 29 faces (baked)
FEATURE [Part::Feature] Chamfer122  label="ISO4032-Hex-Nut-M006"
  Placement = pos=(-299.35,47.69,10) rot=(0,0,1;0rad)
  shape: bbox 6.35 x 2.4 x 6.35 mm, 29 faces (baked)
FEATURE [Part::Feature] Chamfer123  label="ISO4762_Hex_screw-M3x16"
  Placement = pos=(-299.35,37.19,20) rot=(0.57735,0.57735,-0.57735;2.0944rad)
  shape: bbox 5.5 x 19 x 5.5 mm, 16 faces (baked)
FEATURE [Part::Feature] Compound001  label="Servo-Futaba-3003-ready001"
  Placement = pos=(-274.9,69.49,14.95) rot=(1,0,0;1.5708rad)
  shape: bbox 57.75 x 41.74 x 20 mm, 378 faces, 4 solids (baked)
FEATURE [Part::Feature] Chamfer124  label="ISO4762_Hex_screw-M3x017"
  Placement = pos=(-299.35,37.29,10) rot=(0.57735,0.57735,-0.57735;2.0944rad)
  shape: bbox 5.5 x 19 x 5.5 mm, 16 faces (baked)
FEATURE [Part::Feature] Chamfer125  label="ISO4762_Hex_screw-M3x018"
  Placement = pos=(-250.35,37.29,10) rot=(0.57735,0.57735,-0.57735;2.0944rad)
  shape: bbox 5.5 x 19 x 5.5 mm, 16 faces (baked)
FEATURE [Part::Feature] Chamfer126  label="ISO4762_Hex_screw-M3x019"
  Placement = pos=(-250.35,37.29,20) rot=(0.57735,0.57735,-0.57735;2.0944rad)
  shape: bbox 5.5 x 19 x 5.5 mm, 16 faces (baked)
FEATURE [Part::Feature] Fillet018013007  label="rounded-horn003"
  Placement = pos=(-265.45,52.9,64.75) rot=(-0.57735,0.57735,-0.57735;2.0944rad)
  shape: bbox 21 x 21 x 6.2 mm, 65 faces (baked)
FEATURE [Part::Feature] Fillet018013008  label="horn-screw009"
  Placement = pos=(-265.45,45.45,59.15) rot=(0,0.707107,-0.707107;3.14159rad)
  shape: bbox 4.8 x 4.8 x 5.5 mm, 21 faces (baked)
FEATURE [Part::Feature] Fillet018013009  label="horn-screw010"
  Placement = pos=(-272.9,55.245,59.15) rot=(0,0.707107,-0.707107;3.14159rad)
  shape: bbox 4.8 x 4.8 x 5.5 mm, 21 faces (baked)
FEATURE [Part::Feature] Fillet018013010  label="horn-screw011"
  Placement = pos=(-258,55.995,59.15) rot=(0,0.707107,-0.707107;3.14159rad)
  shape: bbox 4.8 x 4.8 x 5.5 mm, 21 faces (baked)
FEATURE [Part::Feature] Fillet018013011  label="rounded-horn002"
  Placement = pos=(-265.45,31.4,14.95) rot=(0.707107,0,-0.707107;3.14159rad)
  shape: bbox 21 x 6.2 x 21 mm, 65 faces (baked)
FEATURE [Part::Feature] Fillet018013012  label="horn-screw006"
  Placement = pos=(-265.45,25.8,22.4) rot=(0.707107,0,0.707107;3.14159rad)
  shape: bbox 4.8 x 5.5 x 4.8 mm, 21 faces (baked)
FEATURE [Part::Feature] Fillet018013013  label="horn-screw007"
  Placement = pos=(-258,25.8,11.855) rot=(0.707107,0,0.707107;3.14159rad)
  shape: bbox 4.8 x 5.5 x 4.8 mm, 21 faces (baked)
FEATURE [Part::Feature] Fillet018013014  label="horn-screw008"
  Placement = pos=(-272.9,25.8,11.855) rot=(0.707107,0,0.707107;3.14159rad)
  shape: bbox 4.8 x 5.5 x 4.8 mm, 21 faces (baked)
FEATURE [Part::Feature] Cut110  label="Shaft-bolt001"
  Placement = pos=(-265.402,52.9083,67.75) rot=(0.707107,-0.707107,0;3.14159rad)
  shape: bbox 5.38 x 5.38 x 9.391 mm, 18 faces (baked)
FEATURE [Part::Feature] Cut111  label="Shaft-bolt002"
  Placement = pos=(-212.402,52.9083,67.75) rot=(0.707107,-0.707107,0;3.14159rad)
  shape: bbox 5.38 x 5.38 x 9.391 mm, 18 faces (baked)
FEATURE [Part::Feature] Fillet018013015  label="horn-screw005"
  Placement = pos=(-219.9,26,11.855) rot=(0.707107,0,0.707107;3.14159rad)
  shape: bbox 4.8 x 5.5 x 4.8 mm, 21 faces (baked)
FEATURE [Part::Feature] Fillet018013016  label="horn-screw004"
  Placement = pos=(-212.45,26,22.4) rot=(0.707107,0,0.707107;3.14159rad)
  shape: bbox 4.8 x 5.5 x 4.8 mm, 21 faces (baked)
FEATURE [Part::Feature] Fillet018013017  label="horn-screw003"
  Placement = pos=(-205,26,11.855) rot=(0.707107,0,0.707107;3.14159rad)
  shape: bbox 4.8 x 5.5 x 4.8 mm, 21 faces (baked)
FEATURE [Part::Feature] Fillet018013018  label="horn-screw002"
  Placement = pos=(-219.9,55.245,59.15) rot=(0,0.707107,-0.707107;3.14159rad)
  shape: bbox 4.8 x 4.8 x 5.5 mm, 21 faces (baked)
FEATURE [Part::Feature] Fillet018013019  label="horn-screw001"
  Placement = pos=(-212.45,45.45,59.15) rot=(0,0.707107,-0.707107;3.14159rad)
  shape: bbox 4.8 x 4.8 x 5.5 mm, 21 faces (baked)
FEATURE [Part::Feature] Fillet018013020  label="horn-screw"
  Placement = pos=(-205,55.995,59.15) rot=(0,0.707107,-0.707107;3.14159rad)
  shape: bbox 4.8 x 4.8 x 5.5 mm, 21 faces (baked)
FEATURE [Part::Feature] Fillet018013021  label="rounded-horn001"
  Placement = pos=(-212.45,52.9,64.75) rot=(-0.57735,0.57735,-0.57735;2.0944rad)
  shape: bbox 21 x 21 x 6.2 mm, 65 faces (baked)
FEATURE [Part::Feature] Fillet018013022  label="rounded-horn"
  Placement = pos=(-212.45,31.6,14.95) rot=(0.707107,0,-0.707107;3.14159rad)
  shape: bbox 21 x 6.2 x 21 mm, 65 faces (baked)
FEATURE [Part::Feature] Chamfer127  label="ISO4762_Hex_screw-M3x10"
  Placement = pos=(-246,80.8,113.94) rot=(0.57735,0.57735,-0.57735;2.0944rad)
  shape: bbox 5.5 x 13 x 5.5 mm, 16 faces (baked)
FEATURE [Part::Feature] Chamfer128  label="ISO4762_Hex_screw-M3x027"
  Placement = pos=(-246,80.8,93.94) rot=(0.57735,0.57735,-0.57735;2.0944rad)
  shape: bbox 5.5 x 13 x 5.5 mm, 16 faces (baked)
FEATURE [Part::Feature] Chamfer129  label="ISO4762_Hex_screw-M3x024"
  Placement = pos=(-226,80.8,113.94) rot=(0.57735,0.57735,-0.57735;2.0944rad)
  shape: bbox 5.5 x 13 x 5.5 mm, 16 faces (baked)
FEATURE [Part::Feature] Chamfer130  label="ISO4032-Hex-Nut-M012"
  Placement = pos=(-246,87.5,113.94) rot=(0,0,1;0rad)
  shape: bbox 6.35 x 2.4 x 6.35 mm, 29 faces (baked)
FEATURE [Part::Feature] Chamfer131  label="ISO4762_Hex_screw-M3x025"
  Placement = pos=(-246,80.8,93.94) rot=(0.57735,0.57735,-0.57735;2.0944rad)
  shape: bbox 5.5 x 13 x 5.5 mm, 16 faces (baked)
FEATURE [Part::Feature] Chamfer132  label="ISO4032-Hex-Nut-M013"
  Placement = pos=(-226,87.5,93.94) rot=(0,0,1;0rad)
  shape: bbox 6.35 x 2.4 x 6.35 mm, 29 faces (baked)
FEATURE [Part::Feature] Chamfer133  label="ISO4762_Hex_screw-M3x026"
  Placement = pos=(-226,80.8,93.94) rot=(0.57735,0.57735,-0.57735;2.0944rad)
  shape: bbox 5.5 x 13 x 5.5 mm, 16 faces (baked)
FEATURE [Part::Feature] Chamfer134  label="ISO4032-Hex-Nut-M014"
  Placement = pos=(-246,87.5,93.94) rot=(0,0,1;0rad)
  shape: bbox 6.35 x 2.4 x 6.35 mm, 29 faces (baked)
FEATURE [Part::Feature] Chamfer135  label="ISO4032-Hex-Nut-M011"
  Placement = pos=(-226,87.5,113.94) rot=(0,0,1;0rad)
  shape: bbox 6.35 x 2.4 x 6.35 mm, 29 faces (baked)
FEATURE [Part::Feature] Chamfer136  label="ISO4032-Hex-Nut-M020"
  Placement = pos=(-207.5,19,77.04) rot=(0.57735,-0.57735,-0.57735;2.0944rad)
  shape: bbox 6.35 x 6.35 x 2.4 mm, 29 faces (baked)
FEATURE [Part::Feature] Chamfer137  label="ISO4762_Hex_screw-M3x033"
  Placement = pos=(-217.5,19,68.54) rot=(0.707107,-0.707107,0;3.14159rad)
  shape: bbox 5.5 x 5.5 x 15 mm, 16 faces (baked)
FEATURE [Part::Feature] Chamfer138  label="ISO4762_Hex_screw-M3x030"
  Placement = pos=(-270.5,68,68.54) rot=(0.707107,-0.707107,0;3.14159rad)
  shape: bbox 5.5 x 5.5 x 15 mm, 16 faces (baked)
FEATURE [Part::Feature] Chamfer139  label="ISO4762_Hex_screw-M3x031"
  Placement = pos=(-217.5,68,68.54) rot=(0.707107,-0.707107,0;3.14159rad)
  shape: bbox 5.5 x 5.5 x 15 mm, 16 faces (baked)
FEATURE [Part::Feature] Chamfer140  label="ISO4762_Hex_screw-M3x032"
  Placement = pos=(-207.5,68,68.54) rot=(0.707107,-0.707107,0;3.14159rad)
  shape: bbox 5.5 x 5.5 x 15 mm, 16 faces (baked)
FEATURE [Part::Feature] Chamfer141  label="ISO4032-Hex-Nut-M019"
  Placement = pos=(-217.5,19,77.04) rot=(0.57735,-0.57735,-0.57735;2.0944rad)
  shape: bbox 6.35 x 6.35 x 2.4 mm, 29 faces (baked)
FEATURE [Part::Feature] Chamfer142  label="ISO4762_Hex_screw-M3x029"
  Placement = pos=(-260.5,68,68.54) rot=(0.707107,-0.707107,0;3.14159rad)
  shape: bbox 5.5 x 5.5 x 15 mm, 16 faces (baked)
FEATURE [Part::Feature] Chamfer143  label="ISO4032-Hex-Nut-M018"
  Placement = pos=(-270.5,19,77.04) rot=(0.57735,-0.57735,-0.57735;2.0944rad)
  shape: bbox 6.35 x 6.35 x 2.4 mm, 29 faces (baked)
FEATURE [Part::Feature] Chamfer144  label="ISO4762_Hex_screw-M3x12"
  Placement = pos=(-270.5,19,68.54) rot=(0.707107,-0.707107,0;3.14159rad)
  shape: bbox 5.5 x 5.5 x 15 mm, 16 faces (baked)
FEATURE [Part::Feature] Chamfer145  label="ISO4032-Hex-Nut-M017"
  Placement = pos=(-260.5,68,77.04) rot=(0.57735,-0.57735,-0.57735;2.0944rad)
  shape: bbox 6.35 x 6.35 x 2.4 mm, 29 faces (baked)
FEATURE [Part::Feature] Chamfer146  label="ISO4032-Hex-Nut-M023"
  Placement = pos=(-272,78.5,73.94) rot=(0,0,-1;1.5708rad)
  shape: bbox 2.4 x 6.35 x 6.35 mm, 29 faces (baked)
FEATURE [Part::Feature] Chamfer147  label="ISO4762_Hex_screw-M3x028"
  Placement = pos=(-260.5,19,68.54) rot=(0.707107,-0.707107,0;3.14159rad)
  shape: bbox 5.5 x 5.5 x 15 mm, 16 faces (baked)
FEATURE [Part::Feature] Chamfer148  label="ISO4032-Hex-Nut-M022"
  Placement = pos=(-217.5,68,77.04) rot=(0.57735,-0.57735,-0.57735;2.0944rad)
  shape: bbox 6.35 x 6.35 x 2.4 mm, 29 faces (baked)
FEATURE [Part::Feature] Chamfer149  label="ISO4032-Hex-Nut-M021"
  Placement = pos=(-207.5,68,77.04) rot=(0.57735,-0.57735,-0.57735;2.0944rad)
  shape: bbox 6.35 x 6.35 x 2.4 mm, 29 faces (baked)
FEATURE [Part::Feature] Compound002  label="Servo-Futaba-3003-ready003"
  Placement = pos=(-265.45,43.45,102.84) rot=(0.707107,0.707107,0;3.14159rad)
  shape: bbox 20 x 57.75 x 41.74 mm, 378 faces, 4 solids (baked)
FEATURE [Part::Feature] Chamfer150  label="ISO4032-Hex-Nut-M015"
  Placement = pos=(-260.5,19,77.04) rot=(0.57735,-0.57735,-0.57735;2.0944rad)
  shape: bbox 6.35 x 6.35 x 2.4 mm, 29 faces (baked)
FEATURE [Part::Feature] Compound003  label="Servo-Futaba-3003-ready004"
  Placement = pos=(-212.45,43.45,102.84) rot=(0.707107,0.707107,0;3.14159rad)
  shape: bbox 20 x 57.75 x 41.74 mm, 378 faces, 4 solids (baked)
FEATURE [Part::Feature] Chamfer151  label="ISO4762_Hex_screw-M3x034"
  Placement = pos=(-207.5,19,68.54) rot=(0.707107,-0.707107,0;3.14159rad)
  shape: bbox 5.5 x 5.5 x 15 mm, 16 faces (baked)
FEATURE [Part::Feature] Chamfer152  label="ISO4032-Hex-Nut-M016"
  Placement = pos=(-270.5,68,77.04) rot=(0.57735,-0.57735,-0.57735;2.0944rad)
  shape: bbox 6.35 x 6.35 x 2.4 mm, 29 faces (baked)
FEATURE [Part::Feature] Chamfer153  label="ISO4032-Hex-Nut-M024"
  Placement = pos=(-208.2,78.5,73.94) rot=(0,0,-1;1.5708rad)
  shape: bbox 2.4 x 6.35 x 6.35 mm, 29 faces (baked)
FEATURE [Part::Feature] Chamfer154  label="ISO4762_Hex_screw-M3x035"
  Placement = pos=(-307,70.9,128.25) rot=(-1,0,0;1.5708rad)
  shape: bbox 5.5 x 13 x 5.5 mm, 16 faces (baked)
FEATURE [Part::Feature] Chamfer155  label="ISO4762_Hex_screw-M3x036"
  Placement = pos=(-278.9,78.5,73.94) rot=(0.57735,0.57735,-0.57735;4.18879rad)
  shape: bbox 13 x 5.5 x 5.5 mm, 16 faces (baked)
FEATURE [Part::Feature] Pocket007  label="shaft-drill003"
  Placement = pos=(-239,52.75,134.5) rot=(0,1,0;3.14159rad)
  shape: bbox 18.7 x 18.7 x 4.1 mm, 22 faces (baked)
FEATURE [Part::Feature] Pocket008  label="shaft-drill004"
  Placement = pos=(-307,34.6,128.25) rot=(1,0,0;1.5708rad)
  shape: bbox 18.7 x 4.1 x 18.7 mm, 22 faces (baked)
FEATURE [Part::Feature] Chamfer156  label="ISO4762_Hex_screw-M3x037"
  Placement = pos=(-199.1,78.5,73.94) rot=(-0.57735,0.57735,-0.57735;2.0944rad)
  shape: bbox 13 x 5.5 x 5.5 mm, 16 faces (baked)
FEATURE [Part::Feature] Chamfer157  label="ISO4032-Hex-Nut-M025"
  Placement = pos=(-171,61.5,128.25) rot=(0,1,0;0.523599rad)
  shape: bbox 6.35 x 2.4 x 6.35 mm, 29 faces (baked)
FEATURE [Part::Feature] Fillet018013023  label="horn-screw012"
  Placement = pos=(-173,29,121.25) rot=(0.707107,0,0.707107;3.14159rad)
  shape: bbox 4.8 x 5.5 x 4.8 mm, 21 faces (baked)
FEATURE [Part::Feature] Fillet018013024  label="horn-screw013"
  Placement = pos=(-169,29,135.25) rot=(0.707107,0,0.707107;3.14159rad)
  shape: bbox 4.8 x 5.5 x 4.8 mm, 21 faces (baked)
FEATURE [Part::Feature] Fillet018013025  label="horn-screw014"
  Placement = pos=(-171,45.2,108.7) rot=(0.707107,0,0.707107;3.14159rad)
  shape: bbox 4.8 x 5.5 x 4.8 mm, 21 faces (baked)
FEATURE [Part::Feature] Fillet018013026  label="horn-screw015"
  Placement = pos=(-165,29,126.75) rot=(0.707107,0,0.707107;3.14159rad)
  shape: bbox 4.8 x 5.5 x 4.8 mm, 21 faces (baked)
FEATURE [Part::Feature] Fillet018013027  label="horn-screw016"
  Placement = pos=(-171,45.2,136.3) rot=(0.707107,0,0.707107;3.14159rad)
  shape: bbox 4.8 x 5.5 x 4.8 mm, 21 faces (baked)
FEATURE [Part::Feature] Fillet018013028  label="horn-screw017"
  Placement = pos=(-177,29,129.75) rot=(0.707107,0,0.707107;3.14159rad)
  shape: bbox 4.8 x 5.5 x 4.8 mm, 21 faces (baked)
FEATURE [Part::Feature] Fillet018013029  label="horn-screw018"
  Placement = pos=(-234.854,48.1478,131) rot=(-1,0,0;1.5708rad)
  shape: bbox 4.8 x 4.8 x 5.5 mm, 21 faces (baked)
FEATURE [Part::Feature] Fillet018013030  label="horn-screw019"
  Placement = pos=(-307,45.2,108.7) rot=(0.707107,0,0.707107;3.14159rad)
  shape: bbox 4.8 x 5.5 x 4.8 mm, 21 faces (baked)
FEATURE [Part::Feature] Fillet018013031  label="horn-screw020"
  Placement = pos=(-309,29,135.25) rot=(0.707107,0,0.707107;3.14159rad)
  shape: bbox 4.8 x 5.5 x 4.8 mm, 21 faces (baked)
FEATURE [Part::Feature] Fillet018013032  label="horn-screw021"
  Placement = pos=(-305,29,121.25) rot=(0.707107,0,0.707107;3.14159rad)
  shape: bbox 4.8 x 5.5 x 4.8 mm, 21 faces (baked)
FEATURE [Part::Feature] Fillet018013033  label="horn-screw022"
  Placement = pos=(-244.562,48.0616,131) rot=(-1,0,0;1.5708rad)
  shape: bbox 4.8 x 4.8 x 5.5 mm, 21 faces (baked)
FEATURE [Part::Feature] Fillet018013034  label="horn-screw023"
  Placement = pos=(-233.417,57.4313,131) rot=(-1,0,0;1.5708rad)
  shape: bbox 4.8 x 4.8 x 5.5 mm, 21 faces (baked)
FEATURE [Part::Feature] Fillet018013035  label="horn-screw024"
  Placement = pos=(-301,29,129.75) rot=(0.707107,0,0.707107;3.14159rad)
  shape: bbox 4.8 x 5.5 x 4.8 mm, 21 faces (baked)
FEATURE [Part::Feature] Fillet018013036  label="horn-screw025"
  Placement = pos=(-307,45.2,136.3) rot=(0.707107,0,0.707107;3.14159rad)
  shape: bbox 4.8 x 5.5 x 4.8 mm, 21 faces (baked)
FEATURE [Part::Feature] Fillet018013037  label="horn-screw026"
  Placement = pos=(-313,29,126.75) rot=(0.707107,0,0.707107;3.14159rad)
  shape: bbox 4.8 x 5.5 x 4.8 mm, 21 faces (baked)
FEATURE [Part::Feature] Fillet018013038  label="horn-screw027"
  Placement = pos=(-243.125,57.3452,131) rot=(-1,0,0;1.5708rad)
  shape: bbox 4.8 x 4.8 x 5.5 mm, 21 faces (baked)
FEATURE [Part::Feature] Pocket009  label="shaft-drill005"
  Placement = pos=(-190.8,52.75,122.5) rot=(0,1,0;1.5708rad)
  shape: bbox 4.1 x 18.7 x 18.7 mm, 22 faces (baked)
FEATURE [Part::Feature] Pocket010  label="shaft-drill006"
  Placement = pos=(-287.2,52.75,122.5) rot=(0,-1,0;1.5708rad)
  shape: bbox 4.1 x 18.7 x 18.7 mm, 22 faces (baked)
FEATURE [Part::Feature] Fillet018013039  label="horn-screw028"
  Placement = pos=(-291.882,58.3121,127.188) rot=(0,0,1;1.5708rad)
  shape: bbox 5.5 x 4.8 x 4.8 mm, 21 faces (baked)
FEATURE [Part::Feature] Fillet018013040  label="horn-screw029"
  Placement = pos=(-291.882,56.8751,117.905) rot=(0,0,1;1.5708rad)
  shape: bbox 5.5 x 4.8 x 4.8 mm, 21 faces (baked)
FEATURE [Part::Feature] Fillet018013041  label="horn-screw030"
  Placement = pos=(-279,33.25,122) rot=(0,0,1;1.5708rad)
  shape: bbox 5.5 x 4.8 x 4.8 mm, 21 faces (baked)
FEATURE [Part::Feature] Fillet018013042  label="horn-screw031"
  Placement = pos=(-291.882,47.1673,117.819) rot=(0,0,1;1.5708rad)
  shape: bbox 5.5 x 4.8 x 4.8 mm, 21 faces (baked)
FEATURE [Part::Feature] Fillet018013043  label="horn-screw032"
  Placement = pos=(-199,60.75,122) rot=(0,0,-1;1.5708rad)
  shape: bbox 5.5 x 4.8 x 4.8 mm, 21 faces (baked)
FEATURE [Part::Feature] Fillet018013044  label="horn-screw033"
  Placement = pos=(-186.118,56.8751,117.905) rot=(0,0,-1;1.5708rad)
  shape: bbox 5.5 x 4.8 x 4.8 mm, 21 faces (baked)
FEATURE [Part::Feature] Fillet018013045  label="horn-screw034"
  Placement = pos=(-186.118,47.1673,117.819) rot=(0,0,-1;1.5708rad)
  shape: bbox 5.5 x 4.8 x 4.8 mm, 21 faces (baked)
FEATURE [Part::Feature] Fillet018013046  label="horn-screw035"
  Placement = pos=(-186.118,48.6043,127.102) rot=(0,0,-1;1.5708rad)
  shape: bbox 5.5 x 4.8 x 4.8 mm, 21 faces (baked)
FEATURE [Part::Feature] Fillet018013047  label="horn-screw036"
  Placement = pos=(-199,33.25,122) rot=(0,0,-1;1.5708rad)
  shape: bbox 5.5 x 4.8 x 4.8 mm, 21 faces (baked)
FEATURE [Part::Feature] Fillet018013048  label="horn-screw037"
  Placement = pos=(-186.118,58.3121,127.188) rot=(0,0,-1;1.5708rad)
  shape: bbox 5.5 x 4.8 x 4.8 mm, 21 faces (baked)
FEATURE [Part::Feature] Fillet018013049  label="horn-screw038"
  Placement = pos=(-279,60.75,122) rot=(0,0,1;1.5708rad)
  shape: bbox 5.5 x 4.8 x 4.8 mm, 21 faces (baked)
FEATURE [Part::Feature] Fillet018013050  label="horn-screw039"
  Placement = pos=(-291.882,48.6043,127.102) rot=(0,0,1;1.5708rad)
  shape: bbox 5.5 x 4.8 x 4.8 mm, 21 faces (baked)
FEATURE [Part::Feature] Chamfer158  label="ISO4762_Hex_screw-M3x038"
  Placement = pos=(-171,71,128.25) rot=(-1,0,0;1.5708rad)
  shape: bbox 5.5 x 13 x 5.5 mm, 16 faces (baked)
FEATURE [Part::Feature] Pocket012  label="top-cross001"
  Placement = pos=(-283.6,52.75,122.5) rot=(0,-1,0;1.5708rad)
  shape: bbox 6.2 x 3 x 3 mm, 18 faces (baked)
FEATURE [Part::Feature] Pocket013  label="top-cross002"
  Placement = pos=(-171,38.2,128.25) rot=(1,0,0;1.5708rad)
  shape: bbox 3 x 6.2 x 3 mm, 18 faces (baked)
FEATURE [Part::Feature] Pocket014  label="top-cross003"
  Placement = pos=(-194.4,52.75,122.5) rot=(0,1,0;1.5708rad)
  shape: bbox 6.2 x 3 x 3 mm, 18 faces (baked)
FEATURE [Part::Feature] Pocket015  label="top-cross004"
  Placement = pos=(-239,52.75,138.1) rot=(1,0,0;3.14159rad)
  shape: bbox 3 x 3 x 6.2 mm, 18 faces (baked)
FEATURE [Part::Feature] Pocket016  label="top-cross005"
  Placement = pos=(-307,38.2,128.25) rot=(1,0,0;1.5708rad)
  shape: bbox 3 x 6.2 x 3 mm, 18 faces (baked)
FEATURE [App::DocumentObjectGroup] Grupo001  label="generic-components"
  Group = -> [Compound,Chamfer109,Chamfer110,Chamfer111,Chamfer112,Chamfer113,Chamfer114,Chamfer115,Chamfer116,Chamfer117,Chamfer118,Chamfer119,Chamfer120,Chamfer121,Chamfer122,Chamfer123,Compound001,Chamfer124,Chamfer125,Chamfer126,Fillet018013007,Fillet018013008,Fillet018013009,Fillet018013010,Fillet018013011,Fillet018013012,Fillet018013013,Fillet018013014,Cut110,Cut111,Fillet018013015,Fillet018013016,+83 more]
FEATURE [Part::Feature] Cut112  label="pie-D001"
  Placement = pos=(-274.85,69.19,3) rot=(0,0,-1;1.5708rad)
  shape: bbox 58 x 72 x 24 mm, 84 faces (baked)
FEATURE [Part::Feature] Part__Mirroring007015  label="pie-I001"
  Placement = pos=(-202.95,69.39,2) rot=(0,0,-1;1.5708rad)
  shape: bbox 58 x 72 x 24 mm, 84 faces (baked)
FEATURE [Sketcher::SketchObject] Sketch018
  Placement = pos=(70,275,66) rot=(0.707107,0.707107,0;3.14159rad)
  sketch-geometry (20):
    g0: LineSegment StartX=-270.5 StartY=-17 StartZ=0 EndX=-260.5 EndY=-17 EndZ=0
    g1: LineSegment StartX=-260.5 StartY=-17 StartZ=0 EndX=-260.5 EndY=-21 EndZ=0
    g2: LineSegment StartX=-260.5 StartY=-21 StartZ=0 EndX=-270.5 EndY=-21 EndZ=0
    g3: LineSegment StartX=-270.5 StartY=-21 StartZ=0 EndX=-270.5 EndY=-17 EndZ=0
    g4: LineSegment StartX=-217.5 StartY=-17 StartZ=0 EndX=-207.5 EndY=-17 EndZ=0
    g5: LineSegment StartX=-207.5 StartY=-17 StartZ=0 EndX=-207.5 EndY=-21 EndZ=0
    g6: LineSegment StartX=-207.5 StartY=-21 StartZ=0 EndX=-217.5 EndY=-21 EndZ=0
    g7: LineSegment StartX=-217.5 StartY=-21 StartZ=0 EndX=-217.5 EndY=-17 EndZ=0
    g8: LineSegment StartX=-270.5 StartY=-66 StartZ=0 EndX=-260.5 EndY=-66 EndZ=0
    g9: LineSegment StartX=-260.5 StartY=-66 StartZ=0 EndX=-260.5 EndY=-70 EndZ=0
    g10: LineSegment StartX=-260.5 StartY=-70 StartZ=0 EndX=-270.5 EndY=-70 EndZ=0
    g11: LineSegment StartX=-270.5 StartY=-70 StartZ=0 EndX=-270.5 EndY=-66 EndZ=0
    g12: LineSegment StartX=-217.5 StartY=-66 StartZ=0 EndX=-207.5 EndY=-66 EndZ=0
    g13: LineSegment StartX=-207.5 StartY=-66 StartZ=0 EndX=-207.5 EndY=-70 EndZ=0
    g14: LineSegment StartX=-207.5 StartY=-70 StartZ=0 EndX=-217.5 EndY=-70 EndZ=0
    g15: LineSegment StartX=-217.5 StartY=-70 StartZ=0 EndX=-217.5 EndY=-66 EndZ=0
    g16: LineSegment [constr] StartX=-260.5 StartY=-21 StartZ=0 EndX=-217.5 EndY=-21 EndZ=0
    g17: LineSegment [constr] StartX=-217.5 StartY=-21 StartZ=0 EndX=-217.5 EndY=-66 EndZ=0
    g18: LineSegment [constr] StartX=-217.5 StartY=-66 StartZ=0 EndX=-260.5 EndY=-66 EndZ=0
    g19: LineSegment [constr] StartX=-260.5 StartY=-66 StartZ=0 EndX=-260.5 EndY=-21 EndZ=0
  constraints (56):
    c: Coincident(g0,g1)
    c: Coincident(g1,g2)
    c: Coincident(g2,g3)
    c: Coincident(g3,g0)
    c: Horizontal(g0)
    c: Horizontal(g2)
    c: Vertical(g1)
    c: Vertical(g3)
    c: Coincident(g4,g5)
    c: Coincident(g5,g6)
    c: Coincident(g6,g7)
    c: Coincident(g7,g4)
    c: Horizontal(g4)
    c: Horizontal(g6)
    c: Vertical(g5)
    c: Vertical(g7)
    c: Coincident(g8,g9)
    c: Coincident(g9,g10)
    c: Coincident(g10,g11)
    c: Coincident(g11,g8)
    c: Horizontal(g8)
    c: Horizontal(g10)
    c: Vertical(g9)
    c: Vertical(g11)
    c: Coincident(g12,g13)
    c: Coincident(g13,g14)
    c: Coincident(g14,g15)
    c: Coincident(g15,g12)
    c: Horizontal(g12)
    c: Horizontal(g14)
    c: Vertical(g13)
    c: Vertical(g15)
    c: Equal(g15,g9)
    c: Equal(g9,g1)
    c: Equal(g1,g7)
    c: Distance(g3) = 4
    c: Distance(g0) = 10
    c: Equal(g2,g6)
    c: Equal(g6,g8)
    c: Equal(g8,g12)
    c: Coincident(g16,g17)
    c: Coincident(g17,g18)
    c: Coincident(g18,g19)
    c: Coincident(g19,g16)
    c: Horizontal(g16)
    c: Horizontal(g18)
    c: Vertical(g17)
    c: Vertical(g19)
    c: Coincident(g1,g16)
    c: Coincident(g16,g6)
    c: Coincident(g12,g17)
    c: Coincident(g18,g8)
    c: Distance(g18) = 43
    c: Distance(g17) = 45
    c: DistanceX(g-1,g6) = -217.5
    c: DistanceY(g-1,g6) = -21
FEATURE [PartDesign::Pad] Pad013
  Length = 10
  Length2 = 100
  Placement = pos=(70,275,66) rot=(0.707107,0.707107,0;3.14159rad)
  Sketch = -> Sketch018
  Type = 0
FEATURE [Part::Cut] Cut113  label="chassis-src"
  Base = -> Fillet018013
  Placement = pos=(-275,70,2) rot=(0,0,-1;1.5708rad)
  Tool = -> Pad013
FEATURE [Part::FeaturePython] Clone025  label="Clone of chassis-src"  # Draft clone (typed FeaturePython)
  Objects = -> [Cut113]
  Placement = pos=(-275,70,2) rot=(0,0,-1;1.5708rad)
  Scale = (1,1,1)
FEATURE [Sketcher::SketchObject] Sketch019
  Placement = pos=(-119,23.5,141) rot=(0,0,1;1.5708rad)
  sketch-geometry (7):
    g0: Circle CenterX=37 CenterY=120 CenterZ=0 NormalX=0 NormalY=0 NormalZ=1 Radius=1.2
    g1: Circle CenterX=9.5 CenterY=120 CenterZ=0 NormalX=0 NormalY=0 NormalZ=1 Radius=1.2
    g2: LineSegment StartX=35.25 StartY=126.5 StartZ=0 EndX=11.25 EndY=126.5 EndZ=0
    g3: LineSegment StartX=11.25 StartY=126.5 StartZ=0 EndX=11.25 EndY=113.5 EndZ=0
    g4: LineSegment StartX=11.25 StartY=113.5 StartZ=0 EndX=35.25 EndY=113.5 EndZ=0
    g5: LineSegment StartX=35.25 StartY=113.5 StartZ=0 EndX=35.25 EndY=126.5 EndZ=0
    g6: LineSegment [constr] StartX=9.5 StartY=120 StartZ=0 EndX=37 EndY=120 EndZ=0
  constraints (20):
    c: Coincident(g2,g3)
    c: Coincident(g3,g4)
    c: Coincident(g4,g5)
    c: Coincident(g5,g2)
    c: Horizontal(g2)
    c: Horizontal(g4)
    c: Vertical(g3)
    c: Vertical(g5)
    c: Distance(g2) = 24
    c: Distance(g5) = 13
    c: Radius(g1) = 1.2
    c: Equal(g1,g0)
    c: Coincident(g0,g6)
    c: Coincident(g1,g6)
    c: Distance(g6) = 27.5
    c: Horizontal(g6)
    c: DistanceX(g-1,g1) = 9.5
    c: DistanceY(g1) = 120
    c: DistanceY(g1,g3) = -6.5
    c: DistanceX(g1,g2) = 1.75
FEATURE [PartDesign::Pad] Pad014
  Length = 16
  Length2 = 100
  Placement = pos=(-119,23.5,141) rot=(0,0,1;1.5708rad)
  Sketch = -> Sketch019
  Type = 0
FEATURE [Part::Box] Box067  label="Cubo013"
  Height = 15.5
  Length = 14
  Placement = pos=(-246,30,131) rot=(0,0,1;0rad)
  Width = 33.5
FEATURE [Part::Box] Box068  label="Cubo014"
  Height = 29.5
  Length = 14
  Placement = pos=(-246,34.75,132) rot=(0,0,1;0rad)
  Width = 24
FEATURE [Sketcher::SketchObject] Sketch020
  Placement = pos=(-232,0,0) rot=(0.57735,0.57735,0.57735;2.0944rad)
  sketch-geometry (12):
    g0: LineSegment StartX=58.7463 StartY=151.629 StartZ=0 EndX=56.7806 EndY=151.629 EndZ=0
    g1: LineSegment StartX=56.7806 StartY=151.629 StartZ=0 EndX=56.7806 EndY=160.733 EndZ=0
    g2: LineSegment StartX=56.7806 StartY=160.733 StartZ=0 EndX=58.7463 EndY=160.733 EndZ=0
    g3: LineSegment StartX=59.4575 StartY=151.357 StartZ=0 EndX=64.2177 EndY=147.084 EndZ=0
    g4: LineSegment StartX=70.0652 StartY=146.486 StartZ=0 EndX=68.6741 EndY=152.764 EndZ=0
    g5: ArcOfCircle CenterX=58.7463 CenterY=150.564 CenterZ=0 NormalX=0 NormalY=0 NormalZ=1 Radius=10.1685 StartAngle=0.218051 EndAngle=1.5708
    g6: ArcOfCircle CenterX=58.7463 CenterY=150.564 CenterZ=0 NormalX=0 NormalY=0 NormalZ=1 Radius=1.06462 StartAngle=0.839342 EndAngle=1.5708
    g7: LineSegment StartX=65.069 StartY=145.176 StartZ=0 EndX=65.069 EndY=134.871 EndZ=0
    g8: LineSegment StartX=65.069 StartY=134.871 StartZ=0 EndX=70.2829 EndY=134.871 EndZ=0
    g9: LineSegment StartX=70.2829 StartY=134.871 StartZ=0 EndX=70.2829 EndY=144.497 EndZ=0
    g10: ArcOfCircle CenterX=61.0884 CenterY=144.497 CenterZ=0 NormalX=0 NormalY=0 NormalZ=1 Radius=9.19448 StartAngle=0 EndAngle=0.218051
    g11: ArcOfCircle CenterX=62.5052 CenterY=145.176 CenterZ=0 NormalX=0 NormalY=0 NormalZ=1 Radius=2.56379 StartAngle=0 EndAngle=0.839342
  constraints (24):
    c: Horizontal(g0)
    c: Coincident(g0,g1)
    c: Vertical(g1)
    c: Coincident(g1,g2)
    c: Horizontal(g2)
    c: Coincident(g5,g2)
    c: Coincident(g5,g4)
    c: Coincident(g6,g0)
    c: Coincident(g6,g3)
    c: Tangent(g2,g5)
    c: Equal(g0,g6)
    c: Tangent(g5,g4)
    c: Coincident(g5,g6)
    c: Tangent(g6,g3)
    c: Tangent(g6,g0)
    c: Vertical(g7)
    c: Coincident(g7,g8)
    c: Horizontal(g8)
    c: Coincident(g8,g9)
    c: Vertical(g9)
    c: Tangent(g4,g10) = -1.5708
    c: Tangent(g9,g10) = -1.5708
    c: Tangent(g3,g11) = 1.5708
    c: Tangent(g7,g11) = 1.5708
FEATURE [PartDesign::Pad] Pad015
  Length = 14
  Length2 = 100
  Placement = pos=(-232,0,0) rot=(0.57735,0.57735,0.57735;2.0944rad)
  Reversed = true
  Sketch = -> Sketch020
  Type = 0
FEATURE [Part::MultiFuse] Fusion065  label="head-positive-cut"
  Shapes = -> [Box067,Pad015,Pad014,Box068]
FEATURE [Part::Box] Box069  label="Cubo015"
  Height = 7.5
  Length = 5
  Placement = pos=(9,97,127) rot=(0,0,1;0rad)
  Width = 12
FEATURE [Part::Cut] Cut114
  Base = -> Cut100
  Tool = -> Box069
FEATURE [App::DocumentObjectGroup] Grupo  label="src001"
  Group = -> [Cut091,Cut107,Fusion045,Cut113,Cut114]
FEATURE [App::DocumentObjectGroup] Group003  label="original-src"
  Group = -> [Part__Mirroring006,Part__Mirroring007,Group004,Group005,Grupo]
FEATURE [Part::Fillet] Fillet018013051
  Base = -> Cut114
  Edges = 1 edges r=0.5: [Edge83]
FEATURE [Part::FeaturePython] Clone026  label="Clone of arm"  # Draft clone (typed FeaturePython)
  Objects = -> [Fillet018013051]
  Placement = pos=(-275,70,2.5) rot=(0,0,-1;1.5708rad)
  Scale = (1,1,1)
FEATURE [Part::Mirroring] Part__Mirroring007016  label="Clone of arm001"
  Base = (0,0,0)
  Normal = (1,0,0)
  Placement = pos=(-478,0,0) rot=(0,0,1;0rad)
  Source = -> Clone026
FEATURE [Part::Prism] Prism  label="Prisma001"
  Circumradius = 3.3
  Height = 10
  Placement = pos=(18,85,84) rot=(-1,0,0;1.5708rad)
  Polygon = 6
FEATURE [Part::Prism] Prism002  label="Prisma002"
  Circumradius = 3.3
  Height = 10
  Placement = pos=(8,85,84) rot=(-1,0,0;1.5708rad)
  Polygon = 6
FEATURE [Part::Cylinder] Cylinder089  label="Cilindro017"
  Angle = 360
  Height = 32
  Placement = pos=(18,116,84) rot=(-1,0,0;1.5708rad)
  Radius = 3
FEATURE [Part::Cylinder] Cylinder090  label="Cilindro018"
  Angle = 360
  Height = 32
  Placement = pos=(8,116,84) rot=(-1,0,0;1.5708rad)
  Radius = 3
FEATURE [Part::Box] Box070  label="Cubo005"
  Height = 28
  Length = 20
  Placement = pos=(3.5,97.5,79.5) rot=(0,0,1;0rad)
  Width = 16
FEATURE [Part::Cylinder] Cylinder091  label="Cilindro013"
  Angle = 360
  Height = 32
  Placement = pos=(18,90,84) rot=(-1,0,0;1.5708rad)
  Radius = 1.75
FEATURE [Part::Cylinder] Cylinder092  label="Cilindro012"
  Angle = 360
  Height = 32
  Placement = pos=(8,90,84) rot=(-1,0,0;1.5708rad)
  Radius = 1.75
FEATURE [Part::MultiFuse] Fusion066  label="arm-positive-cut"
  Shapes = -> [Prism,Prism002,Cylinder089,Cylinder090,Box070,Cylinder091,Cylinder092]
FEATURE [Part::FeaturePython] Clone027  label="Clone of arm-positive-cut-left"  # Draft clone (typed FeaturePython)
  Objects = -> [Fusion066]
  Placement = pos=(-275,70,2.8) rot=(0,0,-1;1.5708rad)
  Scale = (1,1,1)
FEATURE [Part::Mirroring] Part__Mirroring007017  label="Clone of arm-positive-cut-right"
  Base = (0,0,0)
  Normal = (1,0,0)
  Placement = pos=(-478,0,0) rot=(0,0,1;0rad)
  Source = -> Clone027
FEATURE [Part::Feature] Part__Mirroring007013  label="pata-I001"
  Placement = pos=(-202.95,69.9,1.95) rot=(0,0,-1;1.5708rad)
  shape: bbox 21 x 53 x 59.5 mm, 32 faces (baked)
FEATURE [Part::Feature] Part__Mirroring007014  label="leg-body"
  Placement = pos=(-255.95,69.7,1.95) rot=(0,0,-1;1.5708rad)
  shape: bbox 21 x 53 x 59.5 mm, 32 faces (baked)
FEATURE [App::DocumentObjectGroup] Group017  label="Assembly"
  Group = -> [Fusion043,Part__Mirroring007016,Part__Mirroring007014,Part__Mirroring007013,Part__Mirroring007015,Cut112,Clone025]
FEATURE [Part::Box] Box071  label="Cubo016"
  Height = 50
  Length = 50
  Width = 50
FEATURE [Part::Sphere] Sphere  label="Esfera"
  Angle1 = -90
  Angle2 = 90
  Angle3 = 360
  Placement = pos=(13,2,35) rot=(0,0,1;0rad)
  Radius = 5
FEATURE [Part::Sphere] Sphere001  label="Esfera001"
  Angle1 = -90
  Angle2 = 90
  Angle3 = 360
  Placement = pos=(37,2,35) rot=(0,0,1;0rad)
  Radius = 5
FEATURE [Part::Cut] Cut115
  Base = -> Box071
  Tool = -> Sphere
FEATURE [Part::Cut] Cut116
  Base = -> Cut115
  Tool = -> Sphere001
FEATURE [Part::Box] Box072  label="Cubo001"
  Height = 10
  Length = 20
  Placement = pos=(15,-5,9) rot=(0,0,1;0rad)
  Width = 10
FEATURE [Part::Cut] Cut117
  Base = -> Cut116
  Placement = pos=(0,-9,1) rot=(0,0,1;0rad)
  Tool = -> Box072
FEATURE [Part::Box] Box073  label="Cubo002"
  Height = 44
  Length = 2
  Placement = pos=(50,24,45) rot=(0,0,1;0rad)
  Width = 2
FEATURE [Part::Sphere] Sphere002  label="Esfera002"
  Angle1 = -90
  Angle2 = 90
  Angle3 = 360
  Placement = pos=(51,25,90) rot=(0,0,1;0rad)
  Radius = 2.5
FEATURE [Part::Cylinder] Cylinder093  label="Cilindro024"
  Angle = 360
  Height = 2
  Placement = pos=(50,26,45) rot=(1,0,0;1.5708rad)
  Radius = 2
FEATURE [Mesh::Feature] cabeza_para_imprimir  label="cabeza.para.imprimir"
FEATURE [Mesh::Feature] antena_para_imprimir  label="antena.para.imprimir"
  Placement = pos=(-264,36,138) rot=(0,0,1;0rad)
FEATURE [Part::Box] Box084  label="Cube081"
  Height = 66
  Length = 76
  Placement = pos=(-21,-2,87) rot=(0,0,1;0rad)
  Width = 76
FEATURE [Part::Fillet] Fillet018013052
  Base = -> Box084
  Edges = 8 edges r=3.5: [Edge1,Edge2,Edge3,Edge5,Edge6,Edge7,Edge10,Edge12]
  Placement = pos=(0,0,-24) rot=(0,0,1;0rad)
FEATURE [Part::Cylinder] Cylinder094  label="Cylinder121"
  Angle = 360
  Height = 31
  Placement = pos=(-8.5,11,71.5) rot=(1,0,0;1.5708rad)
  Radius = 1.75
FEATURE [Part::Cylinder] Cylinder095  label="Cylinder122"
  Angle = 360
  Height = 31
  Placement = pos=(-8.5,80,71.5) rot=(1,0,0;1.5708rad)
  Radius = 1.75
FEATURE [Part::Cylinder] Cylinder096  label="Cylinder123"
  Angle = 360
  Height = 31
  Placement = pos=(-4,11,83.5) rot=(1,0,0;1.5708rad)
  Radius = 6
FEATURE [Part::Box] Box085  label="Cube082"
  Height = 11
  Length = 8
  Placement = pos=(-13.5,-13,95) rot=(0,0,1;0rad)
  Width = 24
FEATURE [Part::Cylinder] Cylinder097  label="Cylinder124"
  Angle = 360
  Height = 31
  Placement = pos=(-7,80,89.6) rot=(1,0,0;1.5708rad)
  Radius = 4
FEATURE [Part::Box] Box086  label="Cube083"
  Height = 49
  Length = 17
  Placement = pos=(-14,-2.5,75) rot=(0,0,1;0rad)
  Width = 77
FEATURE [Part::Fillet] Fillet018013053
  Base = -> Box086
  Edges = 12 edges r=2: [Edge1,Edge2,Edge3,Edge4,Edge5,Edge6,Edge7,Edge8,Edge9,Edge10,Edge11,Edge12]
FEATURE [Part::Box] Box087  label="Cubo026"
  Height = 63
  Length = 80
  Placement = pos=(-23,-4,68) rot=(0,0,1;0rad)
  Width = 80
FEATURE [Part::Cut] Cut124
  Base = -> Box087
  Tool = -> Fillet018013052
FEATURE [Part::MultiFuse] Fusion067
  Shapes = -> [Box085,Cylinder096,Cylinder094,Fillet018013053,Cylinder097,Cylinder095]
FEATURE [Part::Cut] Cut125
  Base = -> Cut124
  Tool = -> Fusion067
FEATURE [Sketcher::SketchObject] Sketch021
  Placement = pos=(-0.25,-35,0) rot=(1,0,0;1.5708rad)
  sketch-geometry (7):
    g0: Circle CenterX=37 CenterY=120 CenterZ=0 NormalX=0 NormalY=0 NormalZ=1 Radius=1.2
    g1: Circle CenterX=9.5 CenterY=120 CenterZ=0 NormalX=0 NormalY=0 NormalZ=1 Radius=1.2
    g2: LineSegment StartX=35.25 StartY=126.5 StartZ=0 EndX=11.25 EndY=126.5 EndZ=0
    g3: LineSegment StartX=11.25 StartY=126.5 StartZ=0 EndX=11.25 EndY=113.5 EndZ=0
    g4: LineSegment StartX=11.25 StartY=113.5 StartZ=0 EndX=35.25 EndY=113.5 EndZ=0
    g5: LineSegment StartX=35.25 StartY=113.5 StartZ=0 EndX=35.25 EndY=126.5 EndZ=0
    g6: LineSegment [constr] StartX=9.5 StartY=120 StartZ=0 EndX=37 EndY=120 EndZ=0
  constraints (20):
    c: Coincident(g2,g3)
    c: Coincident(g3,g4)
    c: Coincident(g4,g5)
    c: Coincident(g5,g2)
    c: Horizontal(g2)
    c: Horizontal(g4)
    c: Vertical(g3)
    c: Vertical(g5)
    c: Distance(g2) = 24
    c: Distance(g5) = 13
    c: Radius(g1) = 1.2
    c: Equal(g1,g0)
    c: Coincident(g0,g6)
    c: Coincident(g1,g6)
    c: Distance(g6) = 27.5
    c: Horizontal(g6)
    c: DistanceX(g-1,g1) = 9.5
    c: DistanceY(g1) = 120
    c: DistanceY(g1,g3) = -6.5
    c: DistanceX(g1,g2) = 1.75
FEATURE [PartDesign::Pad] Pad016
  Length = 140
  Length2 = 100
  Placement = pos=(-0.25,-35,0) rot=(1,0,0;1.5708rad)
  Reversed = true
  Sketch = -> Sketch021
  Type = 0
FEATURE [Part::Box] Box088  label="Cubo027"
  Height = 4
  Length = 14
  Placement = pos=(11,75.5,109) rot=(0,0,1;0rad)
  Width = 3
FEATURE [Part::Box] Box089  label="Cubo028"
  Height = 4
  Length = 14
  Placement = pos=(11,75.5,127) rot=(0,0,1;0rad)
  Width = 3
FEATURE [Part::Box] Box090  label="Cubo029"
  Height = 4
  Length = 14
  Placement = pos=(11,-6.5,109) rot=(0,0,1;0rad)
  Width = 3
FEATURE [Part::Box] Box091  label="Cubo030"
  Height = 4
  Length = 14
  Placement = pos=(11,-6.5,127) rot=(0,0,1;0rad)
  Width = 3
FEATURE [Part::Cut] Cut126
  Base = -> Cut125
  Tool = -> Pad016
FEATURE [Part::MultiFuse] Fusion068
  Shapes = -> [Cut126,Box089,Box088,Box090,Box091]
FEATURE [Part::Fillet] Fillet018013054  label="prebody001"
  Base = -> Fusion068
  Edges = 8 edges r=1: [Edge2,Edge4,Edge64,Edge66,Edge160,Edge165,Edge170,Edge174]
FEATURE [Part::Box] Box092  label="Cubo031"
  Height = 4
  Length = 10
  Placement = pos=(13,-11,104) rot=(0,0,1;0rad)
  Width = 94
FEATURE [Part::Cut] Cut127  label="body-src001"
  Base = -> Fillet018013054
  Tool = -> Box092
FEATURE [Part::Box] Box094  label="Cubo033"
  Height = 20
  Length = 50
  Width = 25
FEATURE [Part::Box] Box095  label="Cubo034"
  Height = 6
  Length = 50
  Placement = pos=(-2,0,20) rot=(0,1,0;0.139626rad)
  Width = 25
FEATURE [Part::Box] Box096  label="Cubo035"
  Height = 30
  Length = 30
  Placement = pos=(40,0,30) rot=(0,1,0;1.5708rad)
  Width = 30
FEATURE [Part::Cut] Cut130
  Base = -> Box095
  Tool = -> Box096
FEATURE [Part::Box] Box097  label="Cubo036"
  Height = 10
  Length = 10
  Placement = pos=(-10,0,16) rot=(0,0,1;0rad)
  Width = 25
FEATURE [Part::Cut] Cut131
  Base = -> Cut130
  Tool = -> Box097
FEATURE [Part::Box] Box098  label="Cubo037"
  Height = 3
  Length = 2
  Placement = pos=(48,0,20) rot=(0,0,1;0rad)
  Width = 25
FEATURE [Part::MultiFuse] Fusion071  label="brazo"
  Placement = pos=(0,0,0) rot=(0,0,-1;1.5708rad)
  Shapes = -> [Cut131,Box094,Box098]
FEATURE [Part::Box] Box099  label="Cubo038"
  Height = 3
  Length = 2
  Placement = pos=(0,-48,0) rot=(0.57735,-0.57735,-0.57735;2.0944rad)
  Width = 23
FEATURE [Part::Box] Box100  label="Cubo006"
  Height = 3
  Length = 2
  Placement = pos=(28,-48,0) rot=(0.57735,-0.57735,-0.57735;2.0944rad)
  Width = 23
FEATURE [Part::MultiFuse] Fusion072
  Shapes = -> [Box100,Box099,Fusion071]
FEATURE [Part::Prism] Prism003  label="Prisma003"
  Circumradius = 3.3
  Height = 10
  Placement = pos=(18,85,84) rot=(-1,0,0;1.5708rad)
  Polygon = 6
FEATURE [Part::Prism] Prism004  label="Prisma004"
  Circumradius = 3.3
  Height = 10
  Placement = pos=(8,85,84) rot=(-1,0,0;1.5708rad)
  Polygon = 6
FEATURE [Part::Cylinder] Cylinder103  label="Cilindro030"
  Angle = 360
  Height = 32
  Placement = pos=(18,116,84) rot=(-1,0,0;1.5708rad)
  Radius = 3
FEATURE [Part::Cylinder] Cylinder104  label="Cilindro031"
  Angle = 360
  Height = 32
  Placement = pos=(8,116,84) rot=(-1,0,0;1.5708rad)
  Radius = 3
FEATURE [Part::Box] Box101  label="Cubo039"
  Height = 28
  Length = 20
  Placement = pos=(3.5,97.5,79.5) rot=(0,0,1;0rad)
  Width = 16
FEATURE [Part::Cylinder] Cylinder105  label="Cilindro032"
  Angle = 360
  Height = 32
  Placement = pos=(18,90,84) rot=(-1,0,0;1.5708rad)
  Radius = 1.75
FEATURE [Part::Cylinder] Cylinder106  label="Cilindro033"
  Angle = 360
  Height = 32
  Placement = pos=(8,90,84) rot=(-1,0,0;1.5708rad)
  Radius = 1.75
FEATURE [Part::MultiFuse] Fusion073  label="arm-positive-cut001"
  Placement = pos=(26,-91,-93) rot=(0,0.707107,0.707107;3.14159rad)
  Shapes = -> [Prism003,Prism004,Cylinder103,Cylinder104,Box101,Cylinder105,Cylinder106]
FEATURE [Part::Cut] Cut132  label="Brazo"
  Base = -> Fusion072
  Placement = pos=(-182,44,93) rot=(0.57735,0.57735,0.57735;2.0944rad)
  Tool = -> Fusion073
FEATURE [Part::Box] Box110  label="Cubo048"
  Height = 20
  Length = 50
  Width = 25
FEATURE [Part::Box] Box111  label="Cubo049"
  Height = 6
  Length = 50
  Placement = pos=(-2,0,20) rot=(0,1,0;0.139626rad)
  Width = 25
FEATURE [Part::Box] Box112  label="Cubo050"
  Height = 30
  Length = 30
  Placement = pos=(40,0,30) rot=(0,1,0;1.5708rad)
  Width = 30
FEATURE [Part::Cut] Cut136
  Base = -> Box111
  Tool = -> Box112
FEATURE [Part::Box] Box113  label="Cubo051"
  Height = 10
  Length = 10
  Placement = pos=(-10,0,16) rot=(0,0,1;0rad)
  Width = 25
FEATURE [Part::Cut] Cut137
  Base = -> Cut136
  Tool = -> Box113
FEATURE [Part::Box] Box114  label="Cubo052"
  Height = 3
  Length = 2
  Placement = pos=(48,0,20) rot=(0,0,1;0rad)
  Width = 25
FEATURE [Part::MultiFuse] Fusion077  label="brazo002"
  Placement = pos=(0,0,0) rot=(0,0,-1;1.5708rad)
  Shapes = -> [Cut137,Box110,Box114]
FEATURE [Part::Box] Box115  label="Cubo053"
  Height = 3
  Length = 2
  Placement = pos=(0,-48,0) rot=(0.57735,-0.57735,-0.57735;2.0944rad)
  Width = 23
FEATURE [Part::Box] Box116  label="Cubo054"
  Height = 3
  Length = 2
  Placement = pos=(28,-48,0) rot=(0.57735,-0.57735,-0.57735;2.0944rad)
  Width = 23
FEATURE [Part::MultiFuse] Fusion078
  Shapes = -> [Box116,Box115,Fusion077]
FEATURE [Part::Prism] Prism007  label="Prisma007"
  Circumradius = 3.3
  Height = 10
  Placement = pos=(18,85,84) rot=(-1,0,0;1.5708rad)
  Polygon = 6
FEATURE [Part::Prism] Prism008  label="Prisma008"
  Circumradius = 3.3
  Height = 10
  Placement = pos=(8,85,84) rot=(-1,0,0;1.5708rad)
  Polygon = 6
FEATURE [Part::Cylinder] Cylinder111  label="Cilindro038"
  Angle = 360
  Height = 32
  Placement = pos=(18,116,84) rot=(-1,0,0;1.5708rad)
  Radius = 3
FEATURE [Part::Cylinder] Cylinder112  label="Cilindro039"
  Angle = 360
  Height = 32
  Placement = pos=(8,116,84) rot=(-1,0,0;1.5708rad)
  Radius = 3
FEATURE [Part::Box] Box117  label="Cubo055"
  Height = 28
  Length = 20
  Placement = pos=(3.5,97.5,79.5) rot=(0,0,1;0rad)
  Width = 16
FEATURE [Part::Cylinder] Cylinder113  label="Cilindro040"
  Angle = 360
  Height = 32
  Placement = pos=(18,90,84) rot=(-1,0,0;1.5708rad)
  Radius = 1.75
FEATURE [Part::Cylinder] Cylinder114  label="Cilindro041"
  Angle = 360
  Height = 32
  Placement = pos=(8,90,84) rot=(-1,0,0;1.5708rad)
  Radius = 1.75
FEATURE [Part::MultiFuse] Fusion079  label="arm-positive-cut003"
  Placement = pos=(26,-91,-93) rot=(0,0.707107,0.707107;3.14159rad)
  Shapes = -> [Prism007,Prism008,Cylinder111,Cylinder112,Box117,Cylinder113,Cylinder114]
FEATURE [Part::Cut] Cut138  label="Brazo002"
  Base = -> Fusion078
  Placement = pos=(-297,70,93) rot=(0.57735,-0.57735,-0.57735;2.0944rad)
  Tool = -> Fusion079
FEATURE [Part::Box] Box118  label="Cube084"
  Height = 66
  Length = 76
  Placement = pos=(-21,-2,87) rot=(0,0,1;0rad)
  Width = 76
FEATURE [Part::Fillet] Fillet018013055
  Base = -> Box118
  Edges = 8 edges r=3.5: [Edge1,Edge2,Edge3,Edge5,Edge6,Edge7,Edge10,Edge12]
  Placement = pos=(0,0,-24) rot=(0,0,1;0rad)
FEATURE [Part::Cylinder] Cylinder115  label="Cylinder128"
  Angle = 360
  Height = 31
  Placement = pos=(-8.5,11,71.5) rot=(1,0,0;1.5708rad)
  Radius = 1.75
FEATURE [Part::Cylinder] Cylinder116  label="Cylinder129"
  Angle = 360
  Height = 31
  Placement = pos=(-8.5,80,71.5) rot=(1,0,0;1.5708rad)
  Radius = 1.75
FEATURE [Part::Cylinder] Cylinder117  label="Cylinder130"
  Angle = 360
  Height = 31
  Placement = pos=(-4,11,83.5) rot=(1,0,0;1.5708rad)
  Radius = 6
FEATURE [Part::Box] Box119  label="Cube085"
  Height = 11
  Length = 8
  Placement = pos=(-13.5,-13,95) rot=(0,0,1;0rad)
  Width = 24
FEATURE [Part::Cylinder] Cylinder118  label="Cylinder131"
  Angle = 360
  Height = 31
  Placement = pos=(-7,80,89.6) rot=(1,0,0;1.5708rad)
  Radius = 4
FEATURE [Part::Box] Box120  label="Cube086"
  Height = 49
  Length = 17
  Placement = pos=(-14,-2.5,75) rot=(0,0,1;0rad)
  Width = 77
FEATURE [Part::Fillet] Fillet018013056
  Base = -> Box120
  Edges = 12 edges r=2: [Edge1,Edge2,Edge3,Edge4,Edge5,Edge6,Edge7,Edge8,Edge9,Edge10,Edge11,Edge12]
FEATURE [Part::Box] Box121  label="Cubo056"
  Height = 63
  Length = 80
  Placement = pos=(-23,-4,68) rot=(0,0,1;0rad)
  Width = 80
FEATURE [Part::Cut] Cut139
  Base = -> Box121
  Tool = -> Fillet018013055
FEATURE [Part::MultiFuse] Fusion080
  Shapes = -> [Box119,Cylinder117,Cylinder115,Fillet018013056,Cylinder118,Cylinder116]
FEATURE [Part::Cut] Cut140
  Base = -> Cut139
  Tool = -> Fusion080
FEATURE [Sketcher::SketchObject] Sketch022
  Placement = pos=(-0.25,-35,0) rot=(1,0,0;1.5708rad)
  sketch-geometry (7):
    g0: Circle CenterX=37 CenterY=120 CenterZ=0 NormalX=0 NormalY=0 NormalZ=1 Radius=1.2
    g1: Circle CenterX=9.5 CenterY=120 CenterZ=0 NormalX=0 NormalY=0 NormalZ=1 Radius=1.2
    g2: LineSegment StartX=35.25 StartY=126.5 StartZ=0 EndX=11.25 EndY=126.5 EndZ=0
    g3: LineSegment StartX=11.25 StartY=126.5 StartZ=0 EndX=11.25 EndY=113.5 EndZ=0
    g4: LineSegment StartX=11.25 StartY=113.5 StartZ=0 EndX=35.25 EndY=113.5 EndZ=0
    g5: LineSegment StartX=35.25 StartY=113.5 StartZ=0 EndX=35.25 EndY=126.5 EndZ=0
    g6: LineSegment [constr] StartX=9.5 StartY=120 StartZ=0 EndX=37 EndY=120 EndZ=0
  constraints (20):
    c: Coincident(g2,g3)
    c: Coincident(g3,g4)
    c: Coincident(g4,g5)
    c: Coincident(g5,g2)
    c: Horizontal(g2)
    c: Horizontal(g4)
    c: Vertical(g3)
    c: Vertical(g5)
    c: Distance(g2) = 24
    c: Distance(g5) = 13
    c: Radius(g1) = 1.2
    c: Equal(g1,g0)
    c: Coincident(g0,g6)
    c: Coincident(g1,g6)
    c: Distance(g6) = 27.5
    c: Horizontal(g6)
    c: DistanceX(g-1,g1) = 9.5
    c: DistanceY(g1) = 120
    c: DistanceY(g1,g3) = -6.5
    c: DistanceX(g1,g2) = 1.75
FEATURE [PartDesign::Pad] Pad017
  Length = 140
  Length2 = 100
  Placement = pos=(-0.25,-35,0) rot=(1,0,0;1.5708rad)
  Reversed = true
  Sketch = -> Sketch022
  Type = 0
FEATURE [Part::Box] Box122  label="Cubo057"
  Height = 4
  Length = 14
  Placement = pos=(11,75.5,109) rot=(0,0,1;0rad)
  Width = 3
FEATURE [Part::Box] Box123  label="Cubo058"
  Height = 4
  Length = 14
  Placement = pos=(11,75.5,127) rot=(0,0,1;0rad)
  Width = 3
FEATURE [Part::Box] Box124  label="Cubo059"
  Height = 4
  Length = 14
  Placement = pos=(11,-6.5,109) rot=(0,0,1;0rad)
  Width = 3
FEATURE [Part::Box] Box125  label="Cubo060"
  Height = 4
  Length = 14
  Placement = pos=(11,-6.5,127) rot=(0,0,1;0rad)
  Width = 3
FEATURE [Part::Cut] Cut141
  Base = -> Cut140
  Tool = -> Pad017
FEATURE [Part::MultiFuse] Fusion081
  Shapes = -> [Cut141,Box123,Box122,Box124,Box125]
FEATURE [Part::Fillet] Fillet018013057  label="prebody002"
  Base = -> Fusion081
  Edges = 8 edges r=1: [Edge2,Edge4,Edge64,Edge66,Edge160,Edge165,Edge170,Edge174]
FEATURE [Part::Box] Box126  label="Cubo061"
  Height = 4
  Length = 10
  Placement = pos=(13,-11,104) rot=(0,0,1;0rad)
  Width = 94
FEATURE [Part::Cut] Cut142  label="body-src002"
  Base = -> Fillet018013057
  Tool = -> Box126
FEATURE [Part::Mirroring] Part__Mirroring007018  label="left-shoulder001"
  Base = (0,0,0)
  Normal = (0,1,0)
  Placement = pos=(-478,0,0) rot=(0,0,1;3.14159rad)
FEATURE [Part::Box] Box128  label="Cubo063"
  Height = 4
  Length = 22
  Placement = pos=(-174,71,139) rot=(0,0,1;3.14159rad)
  Width = 42
FEATURE [Part::Fillet] Fillet018013058
  Base = -> Box128
  Edges = 8 edges r=1: [Edge1,Edge2,Edge3,Edge5,Edge6,Edge7,Edge10,Edge12]
FEATURE [Part::Box] Box129  label="Cubo064"
  Height = 37
  Length = 10
  Placement = pos=(-199,67,132) rot=(0,0,1;0.785398rad)
  Width = 10
FEATURE [Part::MultiFuse] Fusion084
  Shapes = -> [Part__Mirroring007018,Fillet018013058]
FEATURE [Part::Cut] Cut145
  Base = -> Fusion084
  Tool = -> Box129
FEATURE [Part::Mirroring] Part__Mirroring007019  label="hombreras"
  Base = (0,0,0)
  Normal = (0,1,0)
  Placement = pos=(-478,0,0) rot=(0,0,1;3.14159rad)
  Source = -> Cut145
FEATURE [Mesh::Feature] cuerpo_imprimir  label="cuerpo.imprimir"
